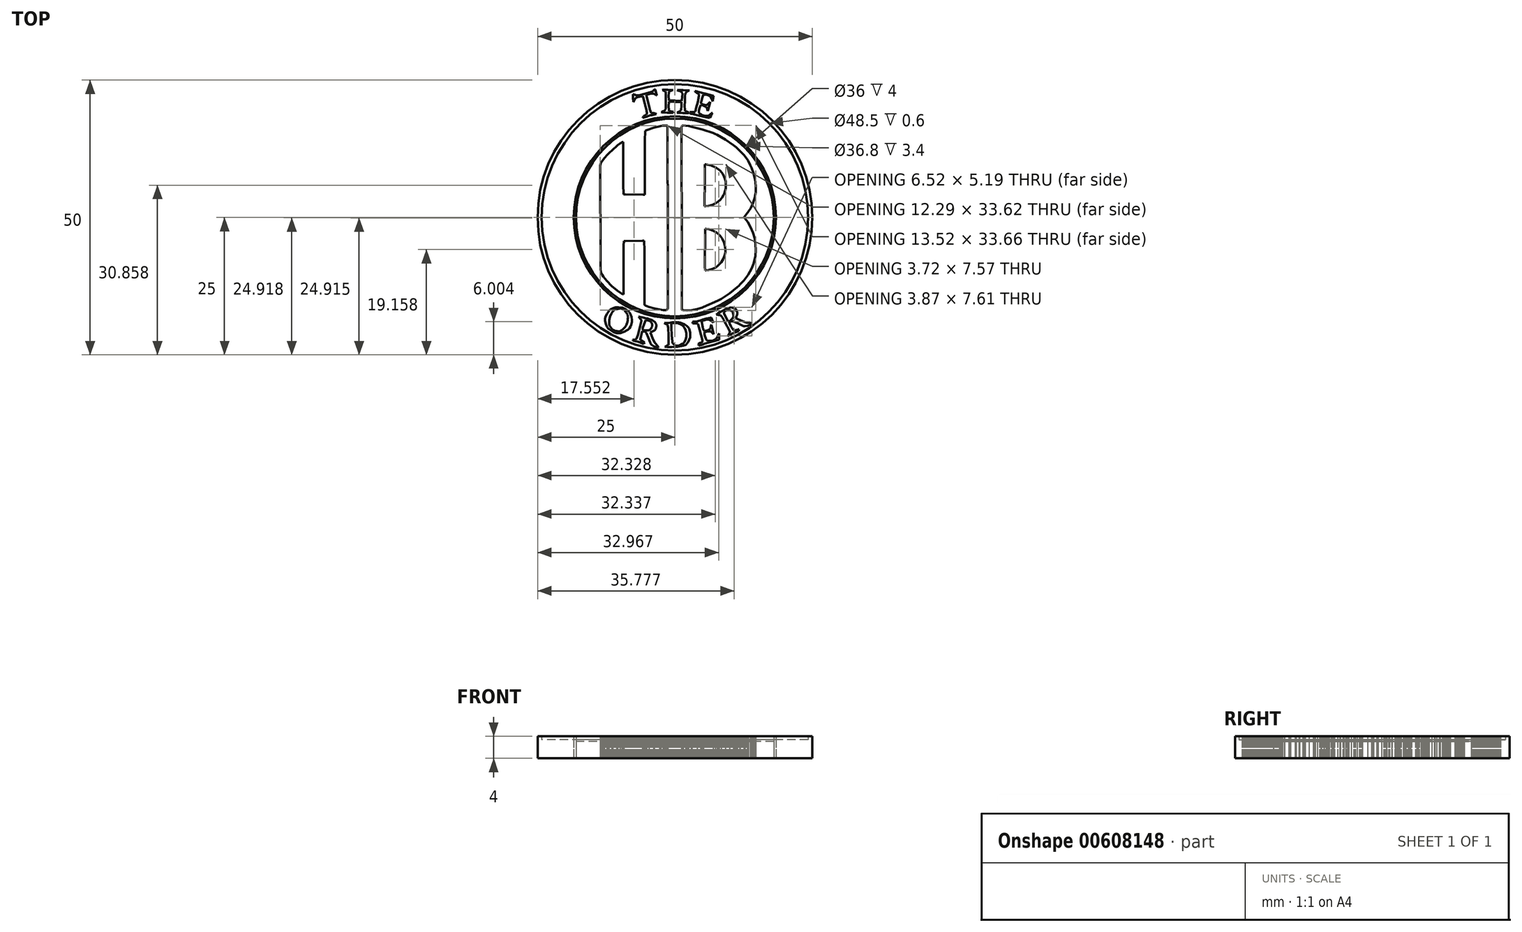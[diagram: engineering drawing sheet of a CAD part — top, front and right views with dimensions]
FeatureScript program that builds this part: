
annotation { "Feature Type Name" : "Feature", "Feature Type Description" : "" }
export const myFeature = defineFeature(function(context is Context, id is Id, definition is map)
    precondition{}
    {
        {
            var Q0;
            Q0=qCreatedBy(makeId("Top.planeOp"),FACE);
            var sketch = newSketch(context, id + "F0", { "sketchPlane" : qUnion([Q0])});
            skLineSegment(sketch, "E0", {"start": v(-4.29, 22.88) * mm, "end": v(-4.22, 22.9) * mm});
            skLineSegment(sketch, "E1", {"start": v(-4.22, 22.9) * mm, "end": v(-3.93, 23.08) * mm});
            skLineSegment(sketch, "E2", {"start": v(-3.93, 23.08) * mm, "end": v(-3.67, 23.3) * mm});
            skLineSegment(sketch, "E3", {"start": v(-3.67, 23.3) * mm, "end": v(-3.61, 23.34) * mm});
            skLineSegment(sketch, "E4", {"start": v(-3.61, 23.34) * mm, "end": v(-3.58, 23.25) * mm});
            skLineSegment(sketch, "E5", {"start": v(-3.58, 23.25) * mm, "end": v(-3.31, 22.3) * mm});
            skLineSegment(sketch, "E6", {"start": v(-3.31, 22.3) * mm, "end": v(-3.3, 22.2) * mm});
            skLineSegment(sketch, "E7", {"start": v(-3.3, 22.2) * mm, "end": v(-3.35, 22.24) * mm});
            skLineSegment(sketch, "E8", {"start": v(-3.35, 22.24) * mm, "end": v(-3.64, 22.4) * mm});
            skLineSegment(sketch, "E9", {"start": v(-3.64, 22.4) * mm, "end": v(-3.95, 22.54) * mm});
            skLineSegment(sketch, "E10", {"start": v(-3.95, 22.54) * mm, "end": v(-4.01, 22.56) * mm});
            skLineSegment(sketch, "E11", {"start": v(-4.01, 22.56) * mm, "end": v(-4.11, 22.55) * mm});
            skLineSegment(sketch, "E12", {"start": v(-4.11, 22.55) * mm, "end": v(-4.6, 22.48) * mm});
            skLineSegment(sketch, "E13", {"start": v(-4.6, 22.48) * mm, "end": v(-5.1, 22.37) * mm});
            skLineSegment(sketch, "E14", {"start": v(-5.1, 22.37) * mm, "end": v(-5.2, 22.35) * mm});
            skLineSegment(sketch, "E15", {"start": v(-5.2, 22.35) * mm, "end": v(-5.15, 22.13) * mm});
            skLineSegment(sketch, "E16", {"start": v(-5.15, 22.13) * mm, "end": v(-4.65, 20) * mm});
            skLineSegment(sketch, "E17", {"start": v(-4.65, 20) * mm, "end": v(-4.6, 19.8) * mm});
            skLineSegment(sketch, "E18", {"start": v(-4.6, 19.8) * mm, "end": v(-4.58, 19.72) * mm});
            skLineSegment(sketch, "E19", {"start": v(-4.58, 19.72) * mm, "end": v(-4.35, 19.05) * mm});
            skLineSegment(sketch, "E20", {"start": v(-4.35, 19.05) * mm, "end": v(-4.32, 18.98) * mm});
            skLineSegment(sketch, "E21", {"start": v(-4.32, 18.98) * mm, "end": v(-4.26, 18.98) * mm});
            skLineSegment(sketch, "E22", {"start": v(-4.26, 18.98) * mm, "end": v(-4.08, 18.98) * mm});
            skLineSegment(sketch, "E23", {"start": v(-4.08, 18.98) * mm, "end": v(-3.84, 18.99) * mm});
            skLineSegment(sketch, "E24", {"start": v(-3.84, 18.99) * mm, "end": v(-3.6, 18.95) * mm});
            skLineSegment(sketch, "E25", {"start": v(-3.6, 18.95) * mm, "end": v(-3.44, 18.86) * mm});
            skLineSegment(sketch, "E26", {"start": v(-3.44, 18.86) * mm, "end": v(-3.4, 18.82) * mm});
            skLineSegment(sketch, "E27", {"start": v(-3.4, 18.82) * mm, "end": v(-3.47, 18.8) * mm});
            skLineSegment(sketch, "E28", {"start": v(-3.47, 18.8) * mm, "end": v(-4.22, 18.64) * mm});
            skLineSegment(sketch, "E29", {"start": v(-4.22, 18.64) * mm, "end": v(-4.3, 18.62) * mm});
            skLineSegment(sketch, "E30", {"start": v(-4.3, 18.62) * mm, "end": v(-4.43, 18.6) * mm});
            skLineSegment(sketch, "E31", {"start": v(-4.43, 18.6) * mm, "end": v(-5.06, 18.39) * mm});
            skLineSegment(sketch, "E32", {"start": v(-5.06, 18.39) * mm, "end": v(-5.7, 18.2) * mm});
            skLineSegment(sketch, "E33", {"start": v(-5.7, 18.2) * mm, "end": v(-5.83, 18.18) * mm});
            skLineSegment(sketch, "E34", {"start": v(-5.83, 18.18) * mm, "end": v(-5.83, 18.22) * mm});
            skLineSegment(sketch, "E35", {"start": v(-5.83, 18.22) * mm, "end": v(-5.8, 18.32) * mm});
            skLineSegment(sketch, "E36", {"start": v(-5.8, 18.32) * mm, "end": v(-5.7, 18.42) * mm});
            skLineSegment(sketch, "E37", {"start": v(-5.7, 18.42) * mm, "end": v(-5.6, 18.5) * mm});
            skLineSegment(sketch, "E38", {"start": v(-5.6, 18.5) * mm, "end": v(-5.46, 18.56) * mm});
            skLineSegment(sketch, "E39", {"start": v(-5.46, 18.56) * mm, "end": v(-5.34, 18.63) * mm});
            skLineSegment(sketch, "E40", {"start": v(-5.34, 18.63) * mm, "end": v(-5.22, 18.7) * mm});
            skLineSegment(sketch, "E41", {"start": v(-5.22, 18.7) * mm, "end": v(-5.14, 18.8) * mm});
            skLineSegment(sketch, "E42", {"start": v(-5.14, 18.8) * mm, "end": v(-5.1, 18.9) * mm});
            skLineSegment(sketch, "E43", {"start": v(-5.1, 18.9) * mm, "end": v(-5.1, 18.94) * mm});
            skLineSegment(sketch, "E44", {"start": v(-5.1, 18.94) * mm, "end": v(-5.1, 19.08) * mm});
            skLineSegment(sketch, "E45", {"start": v(-5.1, 19.08) * mm, "end": v(-5.22, 19.73) * mm});
            skLineSegment(sketch, "E46", {"start": v(-5.22, 19.73) * mm, "end": v(-5.4, 20.37) * mm});
            skLineSegment(sketch, "E47", {"start": v(-5.4, 20.37) * mm, "end": v(-5.43, 20.5) * mm});
            skLineSegment(sketch, "E48", {"start": v(-5.43, 20.5) * mm, "end": v(-5.47, 20.63) * mm});
            skLineSegment(sketch, "E49", {"start": v(-5.47, 20.63) * mm, "end": v(-5.8, 21.98) * mm});
            skLineSegment(sketch, "E50", {"start": v(-5.8, 21.98) * mm, "end": v(-5.84, 22.11) * mm});
            skLineSegment(sketch, "E51", {"start": v(-5.84, 22.11) * mm, "end": v(-5.91, 22.1) * mm});
            skLineSegment(sketch, "E52", {"start": v(-5.91, 22.1) * mm, "end": v(-6.14, 22.06) * mm});
            skLineSegment(sketch, "E53", {"start": v(-6.14, 22.06) * mm, "end": v(-6.44, 22.01) * mm});
            skLineSegment(sketch, "E54", {"start": v(-6.44, 22.01) * mm, "end": v(-6.73, 21.94) * mm});
            skLineSegment(sketch, "E55", {"start": v(-6.73, 21.94) * mm, "end": v(-6.94, 21.85) * mm});
            skLineSegment(sketch, "E56", {"start": v(-6.94, 21.85) * mm, "end": v(-7, 21.81) * mm});
            skLineSegment(sketch, "E57", {"start": v(-7, 21.81) * mm, "end": v(-7.05, 21.78) * mm});
            skLineSegment(sketch, "E58", {"start": v(-7.05, 21.78) * mm, "end": v(-7.17, 21.64) * mm});
            skLineSegment(sketch, "E59", {"start": v(-7.17, 21.64) * mm, "end": v(-7.3, 21.44) * mm});
            skLineSegment(sketch, "E60", {"start": v(-7.3, 21.44) * mm, "end": v(-7.42, 21.24) * mm});
            skLineSegment(sketch, "E61", {"start": v(-7.42, 21.24) * mm, "end": v(-7.51, 21.1) * mm});
            skLineSegment(sketch, "E62", {"start": v(-7.51, 21.1) * mm, "end": v(-7.55, 21.05) * mm});
            skLineSegment(sketch, "E63", {"start": v(-7.55, 21.05) * mm, "end": v(-7.57, 21.16) * mm});
            skLineSegment(sketch, "E64", {"start": v(-7.57, 21.16) * mm, "end": v(-7.63, 21.74) * mm});
            skLineSegment(sketch, "E65", {"start": v(-7.63, 21.74) * mm, "end": v(-7.63, 22.31) * mm});
            skLineSegment(sketch, "E66", {"start": v(-7.63, 22.31) * mm, "end": v(-7.63, 22.43) * mm});
            skLineSegment(sketch, "E67", {"start": v(-7.63, 22.43) * mm, "end": v(-7.56, 22.4) * mm});
            skLineSegment(sketch, "E68", {"start": v(-7.56, 22.4) * mm, "end": v(-7.35, 22.34) * mm});
            skLineSegment(sketch, "E69", {"start": v(-7.35, 22.34) * mm, "end": v(-7.06, 22.26) * mm});
            skLineSegment(sketch, "E70", {"start": v(-7.06, 22.26) * mm, "end": v(-6.78, 22.22) * mm});
            skLineSegment(sketch, "E71", {"start": v(-6.78, 22.22) * mm, "end": v(-6.56, 22.24) * mm});
            skLineSegment(sketch, "E72", {"start": v(-6.56, 22.24) * mm, "end": v(-6.49, 22.27) * mm});
            skLineSegment(sketch, "E73", {"start": v(-6.49, 22.27) * mm, "end": v(-6.3, 22.32) * mm});
            skLineSegment(sketch, "E74", {"start": v(-6.3, 22.32) * mm, "end": v(-4.47, 22.82) * mm});
            skLineSegment(sketch, "E75", {"start": v(-4.47, 22.82) * mm, "end": v(-4.29, 22.88) * mm});
            skLineSegment(sketch, "E76", {"start": v(-2.31, 23.2) * mm, "end": v(-2.15, 23.23) * mm});
            skLineSegment(sketch, "E77", {"start": v(-2.15, 23.23) * mm, "end": v(-1.31, 23.23) * mm});
            skLineSegment(sketch, "E78", {"start": v(-1.31, 23.23) * mm, "end": v(-0.48, 23.21) * mm});
            skLineSegment(sketch, "E79", {"start": v(-0.48, 23.21) * mm, "end": v(-0.31, 23.22) * mm});
            skLineSegment(sketch, "E80", {"start": v(-0.31, 23.22) * mm, "end": v(-0.38, 23.2) * mm});
            skLineSegment(sketch, "E81", {"start": v(-0.38, 23.2) * mm, "end": v(-0.72, 23.07) * mm});
            skLineSegment(sketch, "E82", {"start": v(-0.72, 23.07) * mm, "end": v(-1.04, 22.9) * mm});
            skLineSegment(sketch, "E83", {"start": v(-1.04, 22.9) * mm, "end": v(-1.1, 22.86) * mm});
            skLineSegment(sketch, "E84", {"start": v(-1.1, 22.86) * mm, "end": v(-1.12, 22.73) * mm});
            skLineSegment(sketch, "E85", {"start": v(-1.12, 22.73) * mm, "end": v(-1.13, 22.09) * mm});
            skLineSegment(sketch, "E86", {"start": v(-1.13, 22.09) * mm, "end": v(-1.08, 21.44) * mm});
            skLineSegment(sketch, "E87", {"start": v(-1.08, 21.44) * mm, "end": v(-1.07, 21.31) * mm});
            skLineSegment(sketch, "E88", {"start": v(-1.07, 21.31) * mm, "end": v(-0.88, 21.32) * mm});
            skLineSegment(sketch, "E89", {"start": v(-0.88, 21.32) * mm, "end": v(1.03, 21.24) * mm});
            skLineSegment(sketch, "E90", {"start": v(1.03, 21.24) * mm, "end": v(1.22, 21.25) * mm});
            skLineSegment(sketch, "E91", {"start": v(1.22, 21.25) * mm, "end": v(1.23, 21.36) * mm});
            skLineSegment(sketch, "E92", {"start": v(1.23, 21.36) * mm, "end": v(1.3, 21.95) * mm});
            skLineSegment(sketch, "E93", {"start": v(1.3, 21.95) * mm, "end": v(1.35, 22.53) * mm});
            skLineSegment(sketch, "E94", {"start": v(1.35, 22.53) * mm, "end": v(1.35, 22.65) * mm});
            skLineSegment(sketch, "E95", {"start": v(1.35, 22.65) * mm, "end": v(1.33, 22.7) * mm});
            skLineSegment(sketch, "E96", {"start": v(1.33, 22.7) * mm, "end": v(1.19, 22.85) * mm});
            skLineSegment(sketch, "E97", {"start": v(1.19, 22.85) * mm, "end": v(0.95, 22.97) * mm});
            skLineSegment(sketch, "E98", {"start": v(0.95, 22.97) * mm, "end": v(0.68, 23.06) * mm});
            skLineSegment(sketch, "E99", {"start": v(0.68, 23.06) * mm, "end": v(0.5, 23.13) * mm});
            skLineSegment(sketch, "E100", {"start": v(0.5, 23.13) * mm, "end": v(0.44, 23.17) * mm});
            skLineSegment(sketch, "E101", {"start": v(0.44, 23.17) * mm, "end": v(0.62, 23.21) * mm});
            skLineSegment(sketch, "E102", {"start": v(0.62, 23.21) * mm, "end": v(1.53, 23.2) * mm});
            skLineSegment(sketch, "E103", {"start": v(1.53, 23.2) * mm, "end": v(2.45, 23.14) * mm});
            skLineSegment(sketch, "E104", {"start": v(2.45, 23.14) * mm, "end": v(2.63, 23.15) * mm});
            skLineSegment(sketch, "E105", {"start": v(2.63, 23.15) * mm, "end": v(2.58, 23.12) * mm});
            skLineSegment(sketch, "E106", {"start": v(2.58, 23.12) * mm, "end": v(2.33, 23) * mm});
            skLineSegment(sketch, "E107", {"start": v(2.33, 23) * mm, "end": v(2.08, 22.86) * mm});
            skLineSegment(sketch, "E108", {"start": v(2.08, 22.86) * mm, "end": v(2.04, 22.82) * mm});
            skLineSegment(sketch, "E109", {"start": v(2.04, 22.82) * mm, "end": v(2, 22.74) * mm});
            skLineSegment(sketch, "E110", {"start": v(2, 22.74) * mm, "end": v(1.92, 22.47) * mm});
            skLineSegment(sketch, "E111", {"start": v(1.92, 22.47) * mm, "end": v(1.86, 22.1) * mm});
            skLineSegment(sketch, "E112", {"start": v(1.86, 22.1) * mm, "end": v(1.83, 21.72) * mm});
            skLineSegment(sketch, "E113", {"start": v(1.83, 21.72) * mm, "end": v(1.82, 21.44) * mm});
            skLineSegment(sketch, "E114", {"start": v(1.82, 21.44) * mm, "end": v(1.82, 21.34) * mm});
            skLineSegment(sketch, "E115", {"start": v(1.82, 21.34) * mm, "end": v(1.82, 21.18) * mm});
            skLineSegment(sketch, "E116", {"start": v(1.82, 21.18) * mm, "end": v(1.79, 20.36) * mm});
            skLineSegment(sketch, "E117", {"start": v(1.79, 20.36) * mm, "end": v(1.8, 19.54) * mm});
            skLineSegment(sketch, "E118", {"start": v(1.8, 19.54) * mm, "end": v(1.83, 19.38) * mm});
            skLineSegment(sketch, "E119", {"start": v(1.83, 19.38) * mm, "end": v(1.89, 19.36) * mm});
            skLineSegment(sketch, "E120", {"start": v(1.89, 19.36) * mm, "end": v(2.2, 19.25) * mm});
            skLineSegment(sketch, "E121", {"start": v(2.2, 19.25) * mm, "end": v(2.5, 19.1) * mm});
            skLineSegment(sketch, "E122", {"start": v(2.5, 19.1) * mm, "end": v(2.55, 19.06) * mm});
            skLineSegment(sketch, "E123", {"start": v(2.55, 19.06) * mm, "end": v(2.37, 19.03) * mm});
            skLineSegment(sketch, "E124", {"start": v(2.37, 19.03) * mm, "end": v(1.46, 19) * mm});
            skLineSegment(sketch, "E125", {"start": v(1.46, 19) * mm, "end": v(0.55, 19.05) * mm});
            skLineSegment(sketch, "E126", {"start": v(0.55, 19.05) * mm, "end": v(0.37, 19.06) * mm});
            skLineSegment(sketch, "E127", {"start": v(0.37, 19.06) * mm, "end": v(0.41, 19.09) * mm});
            skLineSegment(sketch, "E128", {"start": v(0.41, 19.09) * mm, "end": v(0.56, 19.17) * mm});
            skLineSegment(sketch, "E129", {"start": v(0.56, 19.17) * mm, "end": v(0.76, 19.27) * mm});
            skLineSegment(sketch, "E130", {"start": v(0.76, 19.27) * mm, "end": v(0.95, 19.39) * mm});
            skLineSegment(sketch, "E131", {"start": v(0.95, 19.39) * mm, "end": v(1.08, 19.5) * mm});
            skLineSegment(sketch, "E132", {"start": v(1.08, 19.5) * mm, "end": v(1.1, 19.54) * mm});
            skLineSegment(sketch, "E133", {"start": v(1.1, 19.54) * mm, "end": v(1.13, 19.66) * mm});
            skLineSegment(sketch, "E134", {"start": v(1.13, 19.66) * mm, "end": v(1.2, 20.3) * mm});
            skLineSegment(sketch, "E135", {"start": v(1.2, 20.3) * mm, "end": v(1.2, 20.93) * mm});
            skLineSegment(sketch, "E136", {"start": v(1.2, 20.93) * mm, "end": v(1.2, 21.06) * mm});
            skLineSegment(sketch, "E137", {"start": v(1.2, 21.06) * mm, "end": v(1, 21.06) * mm});
            skLineSegment(sketch, "E138", {"start": v(1, 21.06) * mm, "end": v(0.04, 21.05) * mm});
            skLineSegment(sketch, "E139", {"start": v(0.04, 21.05) * mm, "end": v(-0.91, 21.08) * mm});
            skLineSegment(sketch, "E140", {"start": v(-0.91, 21.08) * mm, "end": v(-1.1, 21.1) * mm});
            skLineSegment(sketch, "E141", {"start": v(-1.1, 21.1) * mm, "end": v(-1.12, 20.96) * mm});
            skLineSegment(sketch, "E142", {"start": v(-1.12, 20.96) * mm, "end": v(-1.13, 20.25) * mm});
            skLineSegment(sketch, "E143", {"start": v(-1.13, 20.25) * mm, "end": v(-1.1, 19.54) * mm});
            skLineSegment(sketch, "E144", {"start": v(-1.1, 19.54) * mm, "end": v(-1.09, 19.4) * mm});
            skLineSegment(sketch, "E145", {"start": v(-1.09, 19.4) * mm, "end": v(-1.02, 19.39) * mm});
            skLineSegment(sketch, "E146", {"start": v(-1.02, 19.39) * mm, "end": v(-0.31, 19.28) * mm});
            skLineSegment(sketch, "E147", {"start": v(-0.31, 19.28) * mm, "end": v(-0.24, 19.27) * mm});
            skLineSegment(sketch, "E148", {"start": v(-0.24, 19.27) * mm, "end": v(-0.25, 19.25) * mm});
            skLineSegment(sketch, "E149", {"start": v(-0.25, 19.25) * mm, "end": v(-0.35, 19.05) * mm});
            skLineSegment(sketch, "E150", {"start": v(-0.35, 19.05) * mm, "end": v(-0.36, 19.03) * mm});
            skLineSegment(sketch, "E151", {"start": v(-0.36, 19.03) * mm, "end": v(-0.53, 19.07) * mm});
            skLineSegment(sketch, "E152", {"start": v(-0.53, 19.07) * mm, "end": v(-1.41, 19.09) * mm});
            skLineSegment(sketch, "E153", {"start": v(-1.41, 19.09) * mm, "end": v(-2.3, 19.12) * mm});
            skLineSegment(sketch, "E154", {"start": v(-2.3, 19.12) * mm, "end": v(-2.46, 19.17) * mm});
            skLineSegment(sketch, "E155", {"start": v(-2.46, 19.17) * mm, "end": v(-2.4, 19.2) * mm});
            skLineSegment(sketch, "E156", {"start": v(-2.4, 19.2) * mm, "end": v(-2.23, 19.29) * mm});
            skLineSegment(sketch, "E157", {"start": v(-2.23, 19.29) * mm, "end": v(-1.97, 19.4) * mm});
            skLineSegment(sketch, "E158", {"start": v(-1.97, 19.4) * mm, "end": v(-1.77, 19.55) * mm});
            skLineSegment(sketch, "E159", {"start": v(-1.77, 19.55) * mm, "end": v(-1.68, 19.73) * mm});
            skLineSegment(sketch, "E160", {"start": v(-1.68, 19.73) * mm, "end": v(-1.68, 19.8) * mm});
            skLineSegment(sketch, "E161", {"start": v(-1.68, 19.8) * mm, "end": v(-1.66, 20.06) * mm});
            skLineSegment(sketch, "E162", {"start": v(-1.66, 20.06) * mm, "end": v(-1.64, 21.37) * mm});
            skLineSegment(sketch, "E163", {"start": v(-1.64, 21.37) * mm, "end": v(-1.7, 22.68) * mm});
            skLineSegment(sketch, "E164", {"start": v(-1.7, 22.68) * mm, "end": v(-1.7, 22.94) * mm});
            skLineSegment(sketch, "E165", {"start": v(-1.7, 22.94) * mm, "end": v(-1.76, 22.96) * mm});
            skLineSegment(sketch, "E166", {"start": v(-1.76, 22.96) * mm, "end": v(-2.26, 23.19) * mm});
            skLineSegment(sketch, "E167", {"start": v(-2.26, 23.19) * mm, "end": v(-2.31, 23.2) * mm});
            skLineSegment(sketch, "E168", {"start": v(3.67, 23.01) * mm, "end": v(3.82, 23) * mm});
            skLineSegment(sketch, "E169", {"start": v(3.82, 23) * mm, "end": v(4.51, 22.8) * mm});
            skLineSegment(sketch, "E170", {"start": v(4.51, 22.8) * mm, "end": v(5.2, 22.6) * mm});
            skLineSegment(sketch, "E171", {"start": v(5.2, 22.6) * mm, "end": v(5.35, 22.58) * mm});
            skLineSegment(sketch, "E172", {"start": v(5.35, 22.58) * mm, "end": v(5.5, 22.56) * mm});
            skLineSegment(sketch, "E173", {"start": v(5.5, 22.56) * mm, "end": v(6.2, 22.38) * mm});
            skLineSegment(sketch, "E174", {"start": v(6.2, 22.38) * mm, "end": v(6.9, 22.14) * mm});
            skLineSegment(sketch, "E175", {"start": v(6.9, 22.14) * mm, "end": v(7.03, 22.1) * mm});
            skLineSegment(sketch, "E176", {"start": v(7.03, 22.1) * mm, "end": v(7.02, 22.02) * mm});
            skLineSegment(sketch, "E177", {"start": v(7.02, 22.02) * mm, "end": v(6.9, 21.26) * mm});
            skLineSegment(sketch, "E178", {"start": v(6.9, 21.26) * mm, "end": v(6.88, 21.19) * mm});
            skLineSegment(sketch, "E179", {"start": v(6.88, 21.19) * mm, "end": v(6.85, 21.25) * mm});
            skLineSegment(sketch, "E180", {"start": v(6.85, 21.25) * mm, "end": v(6.7, 21.6) * mm});
            skLineSegment(sketch, "E181", {"start": v(6.7, 21.6) * mm, "end": v(6.53, 21.92) * mm});
            skLineSegment(sketch, "E182", {"start": v(6.53, 21.92) * mm, "end": v(6.48, 21.97) * mm});
            skLineSegment(sketch, "E183", {"start": v(6.48, 21.97) * mm, "end": v(6.42, 22.03) * mm});
            skLineSegment(sketch, "E184", {"start": v(6.42, 22.03) * mm, "end": v(6.2, 22.16) * mm});
            skLineSegment(sketch, "E185", {"start": v(6.2, 22.16) * mm, "end": v(5.87, 22.28) * mm});
            skLineSegment(sketch, "E186", {"start": v(5.87, 22.28) * mm, "end": v(5.53, 22.35) * mm});
            skLineSegment(sketch, "E187", {"start": v(5.53, 22.35) * mm, "end": v(5.27, 22.37) * mm});
            skLineSegment(sketch, "E188", {"start": v(5.27, 22.37) * mm, "end": v(5.18, 22.37) * mm});
            skLineSegment(sketch, "E189", {"start": v(5.18, 22.37) * mm, "end": v(5.15, 22.25) * mm});
            skLineSegment(sketch, "E190", {"start": v(5.15, 22.25) * mm, "end": v(4.95, 21.67) * mm});
            skLineSegment(sketch, "E191", {"start": v(4.95, 21.67) * mm, "end": v(4.8, 21.08) * mm});
            skLineSegment(sketch, "E192", {"start": v(4.8, 21.08) * mm, "end": v(4.77, 20.95) * mm});
            skLineSegment(sketch, "E193", {"start": v(4.77, 20.95) * mm, "end": v(4.77, 20.9) * mm});
            skLineSegment(sketch, "E194", {"start": v(4.77, 20.9) * mm, "end": v(4.84, 20.7) * mm});
            skLineSegment(sketch, "E195", {"start": v(4.84, 20.7) * mm, "end": v(5.05, 20.57) * mm});
            skLineSegment(sketch, "E196", {"start": v(5.05, 20.57) * mm, "end": v(5.32, 20.51) * mm});
            skLineSegment(sketch, "E197", {"start": v(5.32, 20.51) * mm, "end": v(5.5, 20.49) * mm});
            skLineSegment(sketch, "E198", {"start": v(5.5, 20.49) * mm, "end": v(5.57, 20.48) * mm});
            skLineSegment(sketch, "E199", {"start": v(5.57, 20.48) * mm, "end": v(5.63, 20.46) * mm});
            skLineSegment(sketch, "E200", {"start": v(5.63, 20.46) * mm, "end": v(5.83, 20.49) * mm});
            skLineSegment(sketch, "E201", {"start": v(5.83, 20.49) * mm, "end": v(6.04, 20.63) * mm});
            skLineSegment(sketch, "E202", {"start": v(6.04, 20.63) * mm, "end": v(6.23, 20.82) * mm});
            skLineSegment(sketch, "E203", {"start": v(6.23, 20.82) * mm, "end": v(6.36, 20.97) * mm});
            skLineSegment(sketch, "E204", {"start": v(6.36, 20.97) * mm, "end": v(6.4, 21) * mm});
            skLineSegment(sketch, "E205", {"start": v(6.4, 21) * mm, "end": v(6.37, 20.87) * mm});
            skLineSegment(sketch, "E206", {"start": v(6.37, 20.87) * mm, "end": v(6, 19.52) * mm});
            skLineSegment(sketch, "E207", {"start": v(6, 19.52) * mm, "end": v(5.96, 19.38) * mm});
            skLineSegment(sketch, "E208", {"start": v(5.96, 19.38) * mm, "end": v(5.94, 19.44) * mm});
            skLineSegment(sketch, "E209", {"start": v(5.94, 19.44) * mm, "end": v(5.86, 19.74) * mm});
            skLineSegment(sketch, "E210", {"start": v(5.86, 19.74) * mm, "end": v(5.76, 20.02) * mm});
            skLineSegment(sketch, "E211", {"start": v(5.76, 20.02) * mm, "end": v(5.73, 20.07) * mm});
            skLineSegment(sketch, "E212", {"start": v(5.73, 20.07) * mm, "end": v(5.68, 20.12) * mm});
            skLineSegment(sketch, "E213", {"start": v(5.68, 20.12) * mm, "end": v(5.5, 20.24) * mm});
            skLineSegment(sketch, "E214", {"start": v(5.5, 20.24) * mm, "end": v(5.25, 20.35) * mm});
            skLineSegment(sketch, "E215", {"start": v(5.25, 20.35) * mm, "end": v(4.98, 20.44) * mm});
            skLineSegment(sketch, "E216", {"start": v(4.98, 20.44) * mm, "end": v(4.77, 20.49) * mm});
            skLineSegment(sketch, "E217", {"start": v(4.77, 20.49) * mm, "end": v(4.7, 20.5) * mm});
            skLineSegment(sketch, "E218", {"start": v(4.7, 20.5) * mm, "end": v(4.67, 20.42) * mm});
            skLineSegment(sketch, "E219", {"start": v(4.67, 20.42) * mm, "end": v(4.57, 20.15) * mm});
            skLineSegment(sketch, "E220", {"start": v(4.57, 20.15) * mm, "end": v(4.46, 19.79) * mm});
            skLineSegment(sketch, "E221", {"start": v(4.46, 19.79) * mm, "end": v(4.4, 19.42) * mm});
            skLineSegment(sketch, "E222", {"start": v(4.4, 19.42) * mm, "end": v(4.39, 19.13) * mm});
            skLineSegment(sketch, "E223", {"start": v(4.39, 19.13) * mm, "end": v(4.4, 19.04) * mm});
            skLineSegment(sketch, "E224", {"start": v(4.4, 19.04) * mm, "end": v(4.44, 18.97) * mm});
            skLineSegment(sketch, "E225", {"start": v(4.44, 18.97) * mm, "end": v(4.62, 18.79) * mm});
            skLineSegment(sketch, "E226", {"start": v(4.62, 18.79) * mm, "end": v(4.92, 18.63) * mm});
            skLineSegment(sketch, "E227", {"start": v(4.92, 18.63) * mm, "end": v(5.26, 18.54) * mm});
            skLineSegment(sketch, "E228", {"start": v(5.26, 18.54) * mm, "end": v(5.51, 18.5) * mm});
            skLineSegment(sketch, "E229", {"start": v(5.51, 18.5) * mm, "end": v(5.6, 18.48) * mm});
            skLineSegment(sketch, "E230", {"start": v(5.6, 18.48) * mm, "end": v(5.68, 18.46) * mm});
            skLineSegment(sketch, "E231", {"start": v(5.68, 18.46) * mm, "end": v(5.94, 18.5) * mm});
            skLineSegment(sketch, "E232", {"start": v(5.94, 18.5) * mm, "end": v(6.25, 18.64) * mm});
            skLineSegment(sketch, "E233", {"start": v(6.25, 18.64) * mm, "end": v(6.54, 18.85) * mm});
            skLineSegment(sketch, "E234", {"start": v(6.54, 18.85) * mm, "end": v(6.75, 19) * mm});
            skLineSegment(sketch, "E235", {"start": v(6.75, 19) * mm, "end": v(6.82, 19.06) * mm});
            skLineSegment(sketch, "E236", {"start": v(6.82, 19.06) * mm, "end": v(6.78, 18.98) * mm});
            skLineSegment(sketch, "E237", {"start": v(6.78, 18.98) * mm, "end": v(6.6, 18.58) * mm});
            skLineSegment(sketch, "E238", {"start": v(6.6, 18.58) * mm, "end": v(6.37, 18.2) * mm});
            skLineSegment(sketch, "E239", {"start": v(6.37, 18.2) * mm, "end": v(6.31, 18.14) * mm});
            skLineSegment(sketch, "E240", {"start": v(6.31, 18.14) * mm, "end": v(6.02, 18.18) * mm});
            skLineSegment(sketch, "E241", {"start": v(6.02, 18.18) * mm, "end": v(4.57, 18.52) * mm});
            skLineSegment(sketch, "E242", {"start": v(4.57, 18.52) * mm, "end": v(3.11, 18.85) * mm});
            skLineSegment(sketch, "E243", {"start": v(3.11, 18.85) * mm, "end": v(2.81, 18.88) * mm});
            skLineSegment(sketch, "E244", {"start": v(2.81, 18.88) * mm, "end": v(2.8, 18.9) * mm});
            skLineSegment(sketch, "E245", {"start": v(2.8, 18.9) * mm, "end": v(2.73, 19.18) * mm});
            skLineSegment(sketch, "E246", {"start": v(2.73, 19.18) * mm, "end": v(2.72, 19.2) * mm});
            skLineSegment(sketch, "E247", {"start": v(2.72, 19.2) * mm, "end": v(2.79, 19.2) * mm});
            skLineSegment(sketch, "E248", {"start": v(2.79, 19.2) * mm, "end": v(3.12, 19.19) * mm});
            skLineSegment(sketch, "E249", {"start": v(3.12, 19.19) * mm, "end": v(3.45, 19.2) * mm});
            skLineSegment(sketch, "E250", {"start": v(3.45, 19.2) * mm, "end": v(3.52, 19.2) * mm});
            skLineSegment(sketch, "E251", {"start": v(3.52, 19.2) * mm, "end": v(3.56, 19.2) * mm});
            skLineSegment(sketch, "E252", {"start": v(3.56, 19.2) * mm, "end": v(3.66, 19.27) * mm});
            skLineSegment(sketch, "E253", {"start": v(3.66, 19.27) * mm, "end": v(3.73, 19.4) * mm});
            skLineSegment(sketch, "E254", {"start": v(3.73, 19.4) * mm, "end": v(3.78, 19.56) * mm});
            skLineSegment(sketch, "E255", {"start": v(3.78, 19.56) * mm, "end": v(3.8, 19.68) * mm});
            skLineSegment(sketch, "E256", {"start": v(3.8, 19.68) * mm, "end": v(3.82, 19.71) * mm});
            skLineSegment(sketch, "E257", {"start": v(3.82, 19.71) * mm, "end": v(3.86, 19.94) * mm});
            skLineSegment(sketch, "E258", {"start": v(3.86, 19.94) * mm, "end": v(4.17, 21.03) * mm});
            skLineSegment(sketch, "E259", {"start": v(4.17, 21.03) * mm, "end": v(4.4, 22.14) * mm});
            skLineSegment(sketch, "E260", {"start": v(4.4, 22.14) * mm, "end": v(4.4, 22.37) * mm});
            skLineSegment(sketch, "E261", {"start": v(4.4, 22.37) * mm, "end": v(4.36, 22.42) * mm});
            skLineSegment(sketch, "E262", {"start": v(4.36, 22.42) * mm, "end": v(4.22, 22.53) * mm});
            skLineSegment(sketch, "E263", {"start": v(4.22, 22.53) * mm, "end": v(4.01, 22.66) * mm});
            skLineSegment(sketch, "E264", {"start": v(4.01, 22.66) * mm, "end": v(3.81, 22.8) * mm});
            skLineSegment(sketch, "E265", {"start": v(3.81, 22.8) * mm, "end": v(3.7, 22.96) * mm});
            skLineSegment(sketch, "E266", {"start": v(3.7, 22.96) * mm, "end": v(3.67, 23.01) * mm});
            skLineSegment(sketch, "E267", {"start": v(1.35, 16.73) * mm, "end": v(1.46, 16.75) * mm});
            skLineSegment(sketch, "E268", {"start": v(1.46, 16.75) * mm, "end": v(1.97, 16.73) * mm});
            skLineSegment(sketch, "E269", {"start": v(1.97, 16.73) * mm, "end": v(2.48, 16.64) * mm});
            skLineSegment(sketch, "E270", {"start": v(2.48, 16.64) * mm, "end": v(2.58, 16.62) * mm});
            skLineSegment(sketch, "E271", {"start": v(2.58, 16.62) * mm, "end": v(2.99, 16.54) * mm});
            skLineSegment(sketch, "E272", {"start": v(2.99, 16.54) * mm, "end": v(5, 16.03) * mm});
            skLineSegment(sketch, "E273", {"start": v(5, 16.03) * mm, "end": v(6.96, 15.35) * mm});
            skLineSegment(sketch, "E274", {"start": v(6.96, 15.35) * mm, "end": v(7.34, 15.19) * mm});
            skLineSegment(sketch, "E275", {"start": v(7.34, 15.19) * mm, "end": v(7.67, 15.04) * mm});
            skLineSegment(sketch, "E276", {"start": v(7.67, 15.04) * mm, "end": v(9.2, 14.18) * mm});
            skLineSegment(sketch, "E277", {"start": v(9.2, 14.18) * mm, "end": v(10.63, 13.16) * mm});
            skLineSegment(sketch, "E278", {"start": v(10.63, 13.16) * mm, "end": v(10.9, 12.94) * mm});
            skLineSegment(sketch, "E279", {"start": v(10.9, 12.94) * mm, "end": v(11.13, 12.75) * mm});
            skLineSegment(sketch, "E280", {"start": v(11.13, 12.75) * mm, "end": v(11.79, 12.15) * mm});
            skLineSegment(sketch, "E281", {"start": v(11.79, 12.15) * mm, "end": v(12.6, 11.3) * mm});
            skLineSegment(sketch, "E282", {"start": v(12.6, 11.3) * mm, "end": v(13.3, 10.34) * mm});
            skLineSegment(sketch, "E283", {"start": v(13.3, 10.34) * mm, "end": v(13.73, 9.56) * mm});
            skLineSegment(sketch, "E284", {"start": v(13.73, 9.56) * mm, "end": v(13.83, 9.28) * mm});
            skLineSegment(sketch, "E285", {"start": v(13.83, 9.28) * mm, "end": v(13.95, 9) * mm});
            skLineSegment(sketch, "E286", {"start": v(13.95, 9) * mm, "end": v(14.26, 8.14) * mm});
            skLineSegment(sketch, "E287", {"start": v(14.26, 8.14) * mm, "end": v(14.56, 6.96) * mm});
            skLineSegment(sketch, "E288", {"start": v(14.56, 6.96) * mm, "end": v(14.71, 5.75) * mm});
            skLineSegment(sketch, "E289", {"start": v(14.71, 5.75) * mm, "end": v(14.73, 4.83) * mm});
            skLineSegment(sketch, "E290", {"start": v(14.73, 4.83) * mm, "end": v(14.7, 4.53) * mm});
            skLineSegment(sketch, "E291", {"start": v(14.7, 4.53) * mm, "end": v(14.67, 4.28) * mm});
            skLineSegment(sketch, "E292", {"start": v(14.67, 4.28) * mm, "end": v(14.53, 3.55) * mm});
            skLineSegment(sketch, "E293", {"start": v(14.53, 3.55) * mm, "end": v(14.24, 2.6) * mm});
            skLineSegment(sketch, "E294", {"start": v(14.24, 2.6) * mm, "end": v(13.81, 1.7) * mm});
            skLineSegment(sketch, "E295", {"start": v(13.81, 1.7) * mm, "end": v(13.4, 1.07) * mm});
            skLineSegment(sketch, "E296", {"start": v(13.4, 1.07) * mm, "end": v(13.24, 0.89) * mm});
            skLineSegment(sketch, "E297", {"start": v(13.24, 0.89) * mm, "end": v(13.19, 0.82) * mm});
            skLineSegment(sketch, "E298", {"start": v(13.19, 0.82) * mm, "end": v(12.63, 0.1) * mm});
            skLineSegment(sketch, "E299", {"start": v(12.63, 0.1) * mm, "end": v(12.57, 0.03) * mm});
            skLineSegment(sketch, "E300", {"start": v(12.57, 0.03) * mm, "end": v(12.75, -0.17) * mm});
            skLineSegment(sketch, "E301", {"start": v(12.75, -0.17) * mm, "end": v(13.23, -0.83) * mm});
            skLineSegment(sketch, "E302", {"start": v(13.23, -0.83) * mm, "end": v(13.78, -1.76) * mm});
            skLineSegment(sketch, "E303", {"start": v(13.78, -1.76) * mm, "end": v(14.2, -2.76) * mm});
            skLineSegment(sketch, "E304", {"start": v(14.2, -2.76) * mm, "end": v(14.5, -3.8) * mm});
            skLineSegment(sketch, "E305", {"start": v(14.5, -3.8) * mm, "end": v(14.68, -4.87) * mm});
            skLineSegment(sketch, "E306", {"start": v(14.68, -4.87) * mm, "end": v(14.73, -5.95) * mm});
            skLineSegment(sketch, "E307", {"start": v(14.73, -5.95) * mm, "end": v(14.63, -7.03) * mm});
            skLineSegment(sketch, "E308", {"start": v(14.63, -7.03) * mm, "end": v(14.47, -7.82) * mm});
            skLineSegment(sketch, "E309", {"start": v(14.47, -7.82) * mm, "end": v(14.4, -8.08) * mm});
            skLineSegment(sketch, "E310", {"start": v(14.4, -8.08) * mm, "end": v(14.3, -8.4) * mm});
            skLineSegment(sketch, "E311", {"start": v(14.3, -8.4) * mm, "end": v(13.96, -9.3) * mm});
            skLineSegment(sketch, "E312", {"start": v(13.96, -9.3) * mm, "end": v(13.33, -10.45) * mm});
            skLineSegment(sketch, "E313", {"start": v(13.33, -10.45) * mm, "end": v(12.55, -11.49) * mm});
            skLineSegment(sketch, "E314", {"start": v(12.55, -11.49) * mm, "end": v(11.89, -12.2) * mm});
            skLineSegment(sketch, "E315", {"start": v(11.89, -12.2) * mm, "end": v(11.65, -12.42) * mm});
            skLineSegment(sketch, "E316", {"start": v(11.65, -12.42) * mm, "end": v(11.37, -12.67) * mm});
            skLineSegment(sketch, "E317", {"start": v(11.37, -12.67) * mm, "end": v(9.95, -13.85) * mm});
            skLineSegment(sketch, "E318", {"start": v(9.95, -13.85) * mm, "end": v(8.4, -14.87) * mm});
            skLineSegment(sketch, "E319", {"start": v(8.4, -14.87) * mm, "end": v(8.08, -15.05) * mm});
            skLineSegment(sketch, "E320", {"start": v(8.08, -15.05) * mm, "end": v(7.82, -15.17) * mm});
            skLineSegment(sketch, "E321", {"start": v(7.82, -15.17) * mm, "end": v(5.18, -16.33) * mm});
            skLineSegment(sketch, "E322", {"start": v(5.18, -16.33) * mm, "end": v(4.91, -16.43) * mm});
            skLineSegment(sketch, "E323", {"start": v(4.91, -16.43) * mm, "end": v(4.69, -16.5) * mm});
            skLineSegment(sketch, "E324", {"start": v(4.69, -16.5) * mm, "end": v(4.02, -16.68) * mm});
            skLineSegment(sketch, "E325", {"start": v(4.02, -16.68) * mm, "end": v(3.1, -16.85) * mm});
            skLineSegment(sketch, "E326", {"start": v(3.1, -16.85) * mm, "end": v(2.19, -16.92) * mm});
            skLineSegment(sketch, "E327", {"start": v(2.19, -16.92) * mm, "end": v(1.5, -16.88) * mm});
            skLineSegment(sketch, "E328", {"start": v(1.5, -16.88) * mm, "end": v(1.27, -16.84) * mm});
            skLineSegment(sketch, "E329", {"start": v(1.27, -16.84) * mm, "end": v(1.25, -15.43) * mm});
            skLineSegment(sketch, "E330", {"start": v(1.25, -15.43) * mm, "end": v(1.24, -1.27) * mm});
            skLineSegment(sketch, "E331", {"start": v(1.24, -1.27) * mm, "end": v(1.23, 0.15) * mm});
            skLineSegment(sketch, "E332", {"start": v(1.23, 0.15) * mm, "end": v(1.24, 0.9) * mm});
            skLineSegment(sketch, "E333", {"start": v(1.24, 0.9) * mm, "end": v(1.2, 8.4) * mm});
            skLineSegment(sketch, "E334", {"start": v(1.2, 8.4) * mm, "end": v(1.2, 9.15) * mm});
            skLineSegment(sketch, "E335", {"start": v(1.2, 9.15) * mm, "end": v(1.2, 10.94) * mm});
            skLineSegment(sketch, "E336", {"start": v(1.2, 10.94) * mm, "end": v(1.2, 15.72) * mm});
            skLineSegment(sketch, "E337", {"start": v(1.2, 15.72) * mm, "end": v(1.2, 16.31) * mm});
            skLineSegment(sketch, "E338", {"start": v(1.2, 16.31) * mm, "end": v(1.21, 16.34) * mm});
            skLineSegment(sketch, "E339", {"start": v(1.21, 16.34) * mm, "end": v(1.21, 16.43) * mm});
            skLineSegment(sketch, "E340", {"start": v(1.21, 16.43) * mm, "end": v(1.22, 16.55) * mm});
            skLineSegment(sketch, "E341", {"start": v(1.22, 16.55) * mm, "end": v(1.26, 16.66) * mm});
            skLineSegment(sketch, "E342", {"start": v(1.26, 16.66) * mm, "end": v(1.33, 16.72) * mm});
            skLineSegment(sketch, "E343", {"start": v(1.33, 16.72) * mm, "end": v(1.35, 16.73) * mm});
            skLineSegment(sketch, "E344", {"start": v(-5.4, 15.76) * mm, "end": v(-5.16, 15.88) * mm});
            skLineSegment(sketch, "E345", {"start": v(-5.16, 15.88) * mm, "end": v(-3.87, 16.34) * mm});
            skLineSegment(sketch, "E346", {"start": v(-3.87, 16.34) * mm, "end": v(-2.52, 16.64) * mm});
            skLineSegment(sketch, "E347", {"start": v(-2.52, 16.64) * mm, "end": v(-2.25, 16.68) * mm});
            skLineSegment(sketch, "E348", {"start": v(-2.25, 16.68) * mm, "end": v(-2.18, 16.7) * mm});
            skLineSegment(sketch, "E349", {"start": v(-2.18, 16.7) * mm, "end": v(-1.41, 16.73) * mm});
            skLineSegment(sketch, "E350", {"start": v(-1.41, 16.73) * mm, "end": v(-1.34, 16.73) * mm});
            skLineSegment(sketch, "E351", {"start": v(-1.34, 16.73) * mm, "end": v(-1.33, 15.8) * mm});
            skLineSegment(sketch, "E352", {"start": v(-1.33, 15.8) * mm, "end": v(-1.32, 6.58) * mm});
            skLineSegment(sketch, "E353", {"start": v(-1.32, 6.58) * mm, "end": v(-1.3, 5.66) * mm});
            skLineSegment(sketch, "E354", {"start": v(-1.3, 5.66) * mm, "end": v(-1.3, 3.81) * mm});
            skLineSegment(sketch, "E355", {"start": v(-1.3, 3.81) * mm, "end": v(-1.3, -14.66) * mm});
            skLineSegment(sketch, "E356", {"start": v(-1.3, -14.66) * mm, "end": v(-1.31, -16.5) * mm});
            skLineSegment(sketch, "E357", {"start": v(-1.31, -16.5) * mm, "end": v(-1.3, -16.55) * mm});
            skLineSegment(sketch, "E358", {"start": v(-1.3, -16.55) * mm, "end": v(-1.34, -16.71) * mm});
            skLineSegment(sketch, "E359", {"start": v(-1.34, -16.71) * mm, "end": v(-1.48, -16.84) * mm});
            skLineSegment(sketch, "E360", {"start": v(-1.48, -16.84) * mm, "end": v(-1.68, -16.9) * mm});
            skLineSegment(sketch, "E361", {"start": v(-1.68, -16.9) * mm, "end": v(-1.84, -16.9) * mm});
            skLineSegment(sketch, "E362", {"start": v(-1.84, -16.9) * mm, "end": v(-1.89, -16.88) * mm});
            skLineSegment(sketch, "E363", {"start": v(-1.89, -16.88) * mm, "end": v(-2.12, -16.86) * mm});
            skLineSegment(sketch, "E364", {"start": v(-2.12, -16.86) * mm, "end": v(-2.83, -16.76) * mm});
            skLineSegment(sketch, "E365", {"start": v(-2.83, -16.76) * mm, "end": v(-3.77, -16.59) * mm});
            skLineSegment(sketch, "E366", {"start": v(-3.77, -16.59) * mm, "end": v(-4.69, -16.32) * mm});
            skLineSegment(sketch, "E367", {"start": v(-4.69, -16.32) * mm, "end": v(-5.35, -16.05) * mm});
            skLineSegment(sketch, "E368", {"start": v(-5.35, -16.05) * mm, "end": v(-5.56, -15.94) * mm});
            skLineSegment(sketch, "E369", {"start": v(-5.56, -15.94) * mm, "end": v(-5.54, -15.22) * mm});
            skLineSegment(sketch, "E370", {"start": v(-5.54, -15.22) * mm, "end": v(-5.52, -8.02) * mm});
            skLineSegment(sketch, "E371", {"start": v(-5.52, -8.02) * mm, "end": v(-5.52, -7.3) * mm});
            skLineSegment(sketch, "E372", {"start": v(-5.52, -7.3) * mm, "end": v(-5.53, -7.05) * mm});
            skLineSegment(sketch, "E373", {"start": v(-5.53, -7.05) * mm, "end": v(-5.54, -5.78) * mm});
            skLineSegment(sketch, "E374", {"start": v(-5.54, -5.78) * mm, "end": v(-5.59, -4.51) * mm});
            skLineSegment(sketch, "E375", {"start": v(-5.59, -4.51) * mm, "end": v(-5.62, -4.26) * mm});
            skLineSegment(sketch, "E376", {"start": v(-5.62, -4.26) * mm, "end": v(-5.93, -4.26) * mm});
            skLineSegment(sketch, "E377", {"start": v(-5.93, -4.26) * mm, "end": v(-9, -4.33) * mm});
            skLineSegment(sketch, "E378", {"start": v(-9, -4.33) * mm, "end": v(-9.3, -4.34) * mm});
            skLineSegment(sketch, "E379", {"start": v(-9.3, -4.34) * mm, "end": v(-9.32, -5.14) * mm});
            skLineSegment(sketch, "E380", {"start": v(-9.32, -5.14) * mm, "end": v(-9.34, -13.22) * mm});
            skLineSegment(sketch, "E381", {"start": v(-9.34, -13.22) * mm, "end": v(-9.36, -14.03) * mm});
            skLineSegment(sketch, "E382", {"start": v(-9.36, -14.03) * mm, "end": v(-9.65, -13.88) * mm});
            skLineSegment(sketch, "E383", {"start": v(-9.65, -13.88) * mm, "end": v(-10.48, -13.34) * mm});
            skLineSegment(sketch, "E384", {"start": v(-10.48, -13.34) * mm, "end": v(-11.49, -12.5) * mm});
            skLineSegment(sketch, "E385", {"start": v(-11.49, -12.5) * mm, "end": v(-12.4, -11.54) * mm});
            skLineSegment(sketch, "E386", {"start": v(-12.4, -11.54) * mm, "end": v(-13.02, -10.77) * mm});
            skLineSegment(sketch, "E387", {"start": v(-13.02, -10.77) * mm, "end": v(-13.2, -10.5) * mm});
            skLineSegment(sketch, "E388", {"start": v(-13.2, -10.5) * mm, "end": v(-13.3, -10.38) * mm});
            skLineSegment(sketch, "E389", {"start": v(-13.3, -10.38) * mm, "end": v(-13.47, -9.96) * mm});
            skLineSegment(sketch, "E390", {"start": v(-13.47, -9.96) * mm, "end": v(-13.55, -9.38) * mm});
            skLineSegment(sketch, "E391", {"start": v(-13.55, -9.38) * mm, "end": v(-13.55, -8.77) * mm});
            skLineSegment(sketch, "E392", {"start": v(-13.55, -8.77) * mm, "end": v(-13.53, -8.33) * mm});
            skLineSegment(sketch, "E393", {"start": v(-13.53, -8.33) * mm, "end": v(-13.53, -8.18) * mm});
            skLineSegment(sketch, "E394", {"start": v(-13.53, -8.18) * mm, "end": v(-13.53, -7.41) * mm});
            skLineSegment(sketch, "E395", {"start": v(-13.53, -7.41) * mm, "end": v(-13.56, 0.25) * mm});
            skLineSegment(sketch, "E396", {"start": v(-13.56, 0.25) * mm, "end": v(-13.57, 1.02) * mm});
            skLineSegment(sketch, "E397", {"start": v(-13.57, 1.02) * mm, "end": v(-13.57, 1.67) * mm});
            skLineSegment(sketch, "E398", {"start": v(-13.57, 1.67) * mm, "end": v(-13.57, 8.2) * mm});
            skLineSegment(sketch, "E399", {"start": v(-13.57, 8.2) * mm, "end": v(-13.58, 8.85) * mm});
            skLineSegment(sketch, "E400", {"start": v(-13.58, 8.85) * mm, "end": v(-13.58, 8.92) * mm});
            skLineSegment(sketch, "E401", {"start": v(-13.58, 8.92) * mm, "end": v(-13.58, 9.14) * mm});
            skLineSegment(sketch, "E402", {"start": v(-13.58, 9.14) * mm, "end": v(-13.6, 9.43) * mm});
            skLineSegment(sketch, "E403", {"start": v(-13.6, 9.43) * mm, "end": v(-13.57, 9.71) * mm});
            skLineSegment(sketch, "E404", {"start": v(-13.57, 9.71) * mm, "end": v(-13.5, 9.92) * mm});
            skLineSegment(sketch, "E405", {"start": v(-13.5, 9.92) * mm, "end": v(-13.46, 9.98) * mm});
            skLineSegment(sketch, "E406", {"start": v(-13.46, 9.98) * mm, "end": v(-13.38, 10.13) * mm});
            skLineSegment(sketch, "E407", {"start": v(-13.38, 10.13) * mm, "end": v(-12.85, 10.8) * mm});
            skLineSegment(sketch, "E408", {"start": v(-12.85, 10.8) * mm, "end": v(-12.26, 11.44) * mm});
            skLineSegment(sketch, "E409", {"start": v(-12.26, 11.44) * mm, "end": v(-12.14, 11.56) * mm});
            skLineSegment(sketch, "E410", {"start": v(-12.14, 11.56) * mm, "end": v(-12.02, 11.7) * mm});
            skLineSegment(sketch, "E411", {"start": v(-12.02, 11.7) * mm, "end": v(-11.34, 12.35) * mm});
            skLineSegment(sketch, "E412", {"start": v(-11.34, 12.35) * mm, "end": v(-10.62, 12.97) * mm});
            skLineSegment(sketch, "E413", {"start": v(-10.62, 12.97) * mm, "end": v(-10.48, 13.1) * mm});
            skLineSegment(sketch, "E414", {"start": v(-10.48, 13.1) * mm, "end": v(-10.4, 13.17) * mm});
            skLineSegment(sketch, "E415", {"start": v(-10.4, 13.17) * mm, "end": v(-9.98, 13.47) * mm});
            skLineSegment(sketch, "E416", {"start": v(-9.98, 13.47) * mm, "end": v(-9.52, 13.71) * mm});
            skLineSegment(sketch, "E417", {"start": v(-9.52, 13.71) * mm, "end": v(-9.42, 13.75) * mm});
            skLineSegment(sketch, "E418", {"start": v(-9.42, 13.75) * mm, "end": v(-9.41, 13.1) * mm});
            skLineSegment(sketch, "E419", {"start": v(-9.41, 13.1) * mm, "end": v(-9.4, 6.7) * mm});
            skLineSegment(sketch, "E420", {"start": v(-9.4, 6.7) * mm, "end": v(-9.39, 6.05) * mm});
            skLineSegment(sketch, "E421", {"start": v(-9.39, 6.05) * mm, "end": v(-9.39, 5.9) * mm});
            skLineSegment(sketch, "E422", {"start": v(-9.39, 5.9) * mm, "end": v(-9.36, 4.33) * mm});
            skLineSegment(sketch, "E423", {"start": v(-9.36, 4.33) * mm, "end": v(-9.34, 4.18) * mm});
            skLineSegment(sketch, "E424", {"start": v(-9.34, 4.18) * mm, "end": v(-9.02, 4.18) * mm});
            skLineSegment(sketch, "E425", {"start": v(-9.02, 4.18) * mm, "end": v(-5.82, 4.14) * mm});
            skLineSegment(sketch, "E426", {"start": v(-5.82, 4.14) * mm, "end": v(-5.5, 4.16) * mm});
            skLineSegment(sketch, "E427", {"start": v(-5.5, 4.16) * mm, "end": v(-5.48, 4.98) * mm});
            skLineSegment(sketch, "E428", {"start": v(-5.48, 4.98) * mm, "end": v(-5.45, 13.17) * mm});
            skLineSegment(sketch, "E429", {"start": v(-5.45, 13.17) * mm, "end": v(-5.45, 13.99) * mm});
            skLineSegment(sketch, "E430", {"start": v(-5.45, 13.99) * mm, "end": v(-5.45, 14.13) * mm});
            skLineSegment(sketch, "E431", {"start": v(-5.45, 14.13) * mm, "end": v(-5.42, 15.61) * mm});
            skLineSegment(sketch, "E432", {"start": v(-5.42, 15.61) * mm, "end": v(-5.4, 15.76) * mm});
            skLineSegment(sketch, "E433", {"start": v(5.48, 9.66) * mm, "end": v(5.66, 9.66) * mm});
            skLineSegment(sketch, "E434", {"start": v(5.66, 9.66) * mm, "end": v(6.56, 9.47) * mm});
            skLineSegment(sketch, "E435", {"start": v(6.56, 9.47) * mm, "end": v(7.4, 9.1) * mm});
            skLineSegment(sketch, "E436", {"start": v(7.4, 9.1) * mm, "end": v(7.57, 9.02) * mm});
            skLineSegment(sketch, "E437", {"start": v(7.57, 9.02) * mm, "end": v(7.75, 8.92) * mm});
            skLineSegment(sketch, "E438", {"start": v(7.75, 8.92) * mm, "end": v(8.23, 8.53) * mm});
            skLineSegment(sketch, "E439", {"start": v(8.23, 8.53) * mm, "end": v(8.74, 7.89) * mm});
            skLineSegment(sketch, "E440", {"start": v(8.74, 7.89) * mm, "end": v(9.09, 7.14) * mm});
            skLineSegment(sketch, "E441", {"start": v(9.09, 7.14) * mm, "end": v(9.24, 6.54) * mm});
            skLineSegment(sketch, "E442", {"start": v(9.24, 6.54) * mm, "end": v(9.26, 6.34) * mm});
            skLineSegment(sketch, "E443", {"start": v(9.26, 6.34) * mm, "end": v(9.27, 6.16) * mm});
            skLineSegment(sketch, "E444", {"start": v(9.27, 6.16) * mm, "end": v(9.25, 5.25) * mm});
            skLineSegment(sketch, "E445", {"start": v(9.25, 5.25) * mm, "end": v(9.02, 4.38) * mm});
            skLineSegment(sketch, "E446", {"start": v(9.02, 4.38) * mm, "end": v(8.94, 4.22) * mm});
            skLineSegment(sketch, "E447", {"start": v(8.94, 4.22) * mm, "end": v(8.88, 4.11) * mm});
            skLineSegment(sketch, "E448", {"start": v(8.88, 4.11) * mm, "end": v(8.56, 3.6) * mm});
            skLineSegment(sketch, "E449", {"start": v(8.56, 3.6) * mm, "end": v(8.17, 3.13) * mm});
            skLineSegment(sketch, "E450", {"start": v(8.17, 3.13) * mm, "end": v(8.08, 3.05) * mm});
            skLineSegment(sketch, "E451", {"start": v(8.08, 3.05) * mm, "end": v(7.94, 2.94) * mm});
            skLineSegment(sketch, "E452", {"start": v(7.94, 2.94) * mm, "end": v(7.48, 2.64) * mm});
            skLineSegment(sketch, "E453", {"start": v(7.48, 2.64) * mm, "end": v(6.82, 2.33) * mm});
            skLineSegment(sketch, "E454", {"start": v(6.82, 2.33) * mm, "end": v(6.13, 2.12) * mm});
            skLineSegment(sketch, "E455", {"start": v(6.13, 2.12) * mm, "end": v(5.58, 2.05) * mm});
            skLineSegment(sketch, "E456", {"start": v(5.58, 2.05) * mm, "end": v(5.4, 2.05) * mm});
            skLineSegment(sketch, "E457", {"start": v(5.4, 2.05) * mm, "end": v(5.4, 2.27) * mm});
            skLineSegment(sketch, "E458", {"start": v(5.4, 2.27) * mm, "end": v(5.4, 4.48) * mm});
            skLineSegment(sketch, "E459", {"start": v(5.4, 4.48) * mm, "end": v(5.42, 4.7) * mm});
            skLineSegment(sketch, "E460", {"start": v(5.42, 4.7) * mm, "end": v(5.43, 5.11) * mm});
            skLineSegment(sketch, "E461", {"start": v(5.43, 5.11) * mm, "end": v(5.47, 9.25) * mm});
            skLineSegment(sketch, "E462", {"start": v(5.47, 9.25) * mm, "end": v(5.48, 9.66) * mm});
            skLineSegment(sketch, "E463", {"start": v(5.5, -2.06) * mm, "end": v(5.68, -2.07) * mm});
            skLineSegment(sketch, "E464", {"start": v(5.68, -2.07) * mm, "end": v(6.22, -2.17) * mm});
            skLineSegment(sketch, "E465", {"start": v(6.22, -2.17) * mm, "end": v(6.91, -2.4) * mm});
            skLineSegment(sketch, "E466", {"start": v(6.91, -2.4) * mm, "end": v(7.55, -2.74) * mm});
            skLineSegment(sketch, "E467", {"start": v(7.55, -2.74) * mm, "end": v(7.98, -3.09) * mm});
            skLineSegment(sketch, "E468", {"start": v(7.98, -3.09) * mm, "end": v(8.1, -3.22) * mm});
            skLineSegment(sketch, "E469", {"start": v(8.1, -3.22) * mm, "end": v(8.24, -3.37) * mm});
            skLineSegment(sketch, "E470", {"start": v(8.24, -3.37) * mm, "end": v(8.6, -3.85) * mm});
            skLineSegment(sketch, "E471", {"start": v(8.6, -3.85) * mm, "end": v(8.93, -4.57) * mm});
            skLineSegment(sketch, "E472", {"start": v(8.93, -4.57) * mm, "end": v(9.13, -5.35) * mm});
            skLineSegment(sketch, "E473", {"start": v(9.13, -5.35) * mm, "end": v(9.19, -5.95) * mm});
            skLineSegment(sketch, "E474", {"start": v(9.19, -5.95) * mm, "end": v(9.18, -6.15) * mm});
            skLineSegment(sketch, "E475", {"start": v(9.18, -6.15) * mm, "end": v(9.18, -6.33) * mm});
            skLineSegment(sketch, "E476", {"start": v(9.18, -6.33) * mm, "end": v(9.08, -6.87) * mm});
            skLineSegment(sketch, "E477", {"start": v(9.08, -6.87) * mm, "end": v(8.8, -7.54) * mm});
            skLineSegment(sketch, "E478", {"start": v(8.8, -7.54) * mm, "end": v(8.4, -8.15) * mm});
            skLineSegment(sketch, "E479", {"start": v(8.4, -8.15) * mm, "end": v(8.06, -8.57) * mm});
            skLineSegment(sketch, "E480", {"start": v(8.06, -8.57) * mm, "end": v(7.93, -8.7) * mm});
            skLineSegment(sketch, "E481", {"start": v(7.93, -8.7) * mm, "end": v(7.8, -8.82) * mm});
            skLineSegment(sketch, "E482", {"start": v(7.8, -8.82) * mm, "end": v(7.4, -9.1) * mm});
            skLineSegment(sketch, "E483", {"start": v(7.4, -9.1) * mm, "end": v(6.8, -9.4) * mm});
            skLineSegment(sketch, "E484", {"start": v(6.8, -9.4) * mm, "end": v(6.15, -9.57) * mm});
            skLineSegment(sketch, "E485", {"start": v(6.15, -9.57) * mm, "end": v(5.65, -9.63) * mm});
            skLineSegment(sketch, "E486", {"start": v(5.65, -9.63) * mm, "end": v(5.48, -9.62) * mm});
            skLineSegment(sketch, "E487", {"start": v(5.48, -9.62) * mm, "end": v(5.47, -9) * mm});
            skLineSegment(sketch, "E488", {"start": v(5.47, -9) * mm, "end": v(5.5, -2.69) * mm});
            skLineSegment(sketch, "E489", {"start": v(5.5, -2.69) * mm, "end": v(5.5, -2.06) * mm});
            skLineSegment(sketch, "E490", {"start": v(-10.95, -16.44) * mm, "end": v(-10.78, -16.4) * mm});
            skLineSegment(sketch, "E491", {"start": v(-10.78, -16.4) * mm, "end": v(-10.25, -16.35) * mm});
            skLineSegment(sketch, "E492", {"start": v(-10.25, -16.35) * mm, "end": v(-9.56, -16.45) * mm});
            skLineSegment(sketch, "E493", {"start": v(-9.56, -16.45) * mm, "end": v(-8.91, -16.73) * mm});
            skLineSegment(sketch, "E494", {"start": v(-8.91, -16.73) * mm, "end": v(-8.48, -17.04) * mm});
            skLineSegment(sketch, "E495", {"start": v(-8.48, -17.04) * mm, "end": v(-8.37, -17.17) * mm});
            skLineSegment(sketch, "E496", {"start": v(-8.37, -17.17) * mm, "end": v(-8.3, -17.28) * mm});
            skLineSegment(sketch, "E497", {"start": v(-8.3, -17.28) * mm, "end": v(-8.1, -17.64) * mm});
            skLineSegment(sketch, "E498", {"start": v(-8.1, -17.64) * mm, "end": v(-7.9, -18.15) * mm});
            skLineSegment(sketch, "E499", {"start": v(-7.9, -18.15) * mm, "end": v(-7.81, -18.68) * mm});
            skLineSegment(sketch, "E500", {"start": v(-7.81, -18.68) * mm, "end": v(-7.83, -19.1) * mm});
            skLineSegment(sketch, "E501", {"start": v(-7.83, -19.1) * mm, "end": v(-7.86, -19.22) * mm});
            skLineSegment(sketch, "E502", {"start": v(-7.86, -19.22) * mm, "end": v(-7.9, -19.3) * mm});
            skLineSegment(sketch, "E503", {"start": v(-7.9, -19.3) * mm, "end": v(-7.97, -19.55) * mm});
            skLineSegment(sketch, "E504", {"start": v(-7.97, -19.55) * mm, "end": v(-8.1, -19.88) * mm});
            skLineSegment(sketch, "E505", {"start": v(-8.1, -19.88) * mm, "end": v(-8.27, -20.18) * mm});
            skLineSegment(sketch, "E506", {"start": v(-8.27, -20.18) * mm, "end": v(-8.44, -20.37) * mm});
            skLineSegment(sketch, "E507", {"start": v(-8.44, -20.37) * mm, "end": v(-8.51, -20.42) * mm});
            skLineSegment(sketch, "E508", {"start": v(-8.51, -20.42) * mm, "end": v(-8.62, -20.5) * mm});
            skLineSegment(sketch, "E509", {"start": v(-8.62, -20.5) * mm, "end": v(-9.24, -20.85) * mm});
            skLineSegment(sketch, "E510", {"start": v(-9.24, -20.85) * mm, "end": v(-9.9, -21.07) * mm});
            skLineSegment(sketch, "E511", {"start": v(-9.9, -21.07) * mm, "end": v(-10.04, -21.1) * mm});
            skLineSegment(sketch, "E512", {"start": v(-10.04, -21.1) * mm, "end": v(-10.13, -21.1) * mm});
            skLineSegment(sketch, "E513", {"start": v(-10.13, -21.1) * mm, "end": v(-10.6, -21.05) * mm});
            skLineSegment(sketch, "E514", {"start": v(-10.6, -21.05) * mm, "end": v(-11.05, -20.94) * mm});
            skLineSegment(sketch, "E515", {"start": v(-11.05, -20.94) * mm, "end": v(-11.14, -20.91) * mm});
            skLineSegment(sketch, "E516", {"start": v(-11.14, -20.91) * mm, "end": v(-11.22, -20.88) * mm});
            skLineSegment(sketch, "E517", {"start": v(-11.22, -20.88) * mm, "end": v(-11.59, -20.64) * mm});
            skLineSegment(sketch, "E518", {"start": v(-11.59, -20.64) * mm, "end": v(-11.94, -20.38) * mm});
            skLineSegment(sketch, "E519", {"start": v(-11.94, -20.38) * mm, "end": v(-12, -20.33) * mm});
            skLineSegment(sketch, "E520", {"start": v(-12, -20.33) * mm, "end": v(-12.11, -20.23) * mm});
            skLineSegment(sketch, "E521", {"start": v(-12.11, -20.23) * mm, "end": v(-12.38, -19.88) * mm});
            skLineSegment(sketch, "E522", {"start": v(-12.38, -19.88) * mm, "end": v(-12.6, -19.35) * mm});
            skLineSegment(sketch, "E523", {"start": v(-12.6, -19.35) * mm, "end": v(-12.7, -18.77) * mm});
            skLineSegment(sketch, "E524", {"start": v(-12.7, -18.77) * mm, "end": v(-12.69, -18.34) * mm});
            skLineSegment(sketch, "E525", {"start": v(-12.69, -18.34) * mm, "end": v(-12.66, -18.2) * mm});
            skLineSegment(sketch, "E526", {"start": v(-12.66, -18.2) * mm, "end": v(-12.62, -18.07) * mm});
            skLineSegment(sketch, "E527", {"start": v(-12.62, -18.07) * mm, "end": v(-12.33, -17.5) * mm});
            skLineSegment(sketch, "E528", {"start": v(-12.33, -17.5) * mm, "end": v(-11.95, -16.97) * mm});
            skLineSegment(sketch, "E529", {"start": v(-11.95, -16.97) * mm, "end": v(-11.86, -16.87) * mm});
            skLineSegment(sketch, "E530", {"start": v(-11.86, -16.87) * mm, "end": v(-11.82, -16.83) * mm});
            skLineSegment(sketch, "E531", {"start": v(-11.82, -16.83) * mm, "end": v(-11.66, -16.72) * mm});
            skLineSegment(sketch, "E532", {"start": v(-11.66, -16.72) * mm, "end": v(-11.43, -16.6) * mm});
            skLineSegment(sketch, "E533", {"start": v(-11.43, -16.6) * mm, "end": v(-11.2, -16.52) * mm});
            skLineSegment(sketch, "E534", {"start": v(-11.2, -16.52) * mm, "end": v(-11, -16.46) * mm});
            skLineSegment(sketch, "E535", {"start": v(-11, -16.46) * mm, "end": v(-10.95, -16.44) * mm});
            skLineSegment(sketch, "E536", {"start": v(8.92, -16.87) * mm, "end": v(9, -16.81) * mm});
            skLineSegment(sketch, "E537", {"start": v(9, -16.81) * mm, "end": v(9.27, -16.67) * mm});
            skLineSegment(sketch, "E538", {"start": v(9.27, -16.67) * mm, "end": v(9.63, -16.52) * mm});
            skLineSegment(sketch, "E539", {"start": v(9.63, -16.52) * mm, "end": v(10, -16.42) * mm});
            skLineSegment(sketch, "E540", {"start": v(10, -16.42) * mm, "end": v(10.3, -16.4) * mm});
            skLineSegment(sketch, "E541", {"start": v(10.3, -16.4) * mm, "end": v(10.4, -16.4) * mm});
            skLineSegment(sketch, "E542", {"start": v(10.4, -16.4) * mm, "end": v(10.49, -16.4) * mm});
            skLineSegment(sketch, "E543", {"start": v(10.49, -16.4) * mm, "end": v(10.75, -16.49) * mm});
            skLineSegment(sketch, "E544", {"start": v(10.75, -16.49) * mm, "end": v(11.03, -16.7) * mm});
            skLineSegment(sketch, "E545", {"start": v(11.03, -16.7) * mm, "end": v(11.23, -17) * mm});
            skLineSegment(sketch, "E546", {"start": v(11.23, -17) * mm, "end": v(11.32, -17.24) * mm});
            skLineSegment(sketch, "E547", {"start": v(11.32, -17.24) * mm, "end": v(11.33, -17.33) * mm});
            skLineSegment(sketch, "E548", {"start": v(11.33, -17.33) * mm, "end": v(11.35, -17.39) * mm});
            skLineSegment(sketch, "E549", {"start": v(11.35, -17.39) * mm, "end": v(11.34, -17.59) * mm});
            skLineSegment(sketch, "E550", {"start": v(11.34, -17.59) * mm, "end": v(11.27, -17.84) * mm});
            skLineSegment(sketch, "E551", {"start": v(11.27, -17.84) * mm, "end": v(11.16, -18.08) * mm});
            skLineSegment(sketch, "E552", {"start": v(11.16, -18.08) * mm, "end": v(11.08, -18.26) * mm});
            skLineSegment(sketch, "E553", {"start": v(11.08, -18.26) * mm, "end": v(11.05, -18.32) * mm});
            skLineSegment(sketch, "E554", {"start": v(11.05, -18.32) * mm, "end": v(11.21, -18.4) * mm});
            skLineSegment(sketch, "E555", {"start": v(11.21, -18.4) * mm, "end": v(12.03, -18.78) * mm});
            skLineSegment(sketch, "E556", {"start": v(12.03, -18.78) * mm, "end": v(12.87, -19.1) * mm});
            skLineSegment(sketch, "E557", {"start": v(12.87, -19.1) * mm, "end": v(13.05, -19.14) * mm});
            skLineSegment(sketch, "E558", {"start": v(13.05, -19.14) * mm, "end": v(13.13, -19.16) * mm});
            skLineSegment(sketch, "E559", {"start": v(13.13, -19.16) * mm, "end": v(13.96, -19.25) * mm});
            skLineSegment(sketch, "E560", {"start": v(13.96, -19.25) * mm, "end": v(14.04, -19.27) * mm});
            skLineSegment(sketch, "E561", {"start": v(14.04, -19.27) * mm, "end": v(13.95, -19.34) * mm});
            skLineSegment(sketch, "E562", {"start": v(13.95, -19.34) * mm, "end": v(13.67, -19.53) * mm});
            skLineSegment(sketch, "E563", {"start": v(13.67, -19.53) * mm, "end": v(13.27, -19.74) * mm});
            skLineSegment(sketch, "E564", {"start": v(13.27, -19.74) * mm, "end": v(12.84, -19.83) * mm});
            skLineSegment(sketch, "E565", {"start": v(12.84, -19.83) * mm, "end": v(12.5, -19.79) * mm});
            skLineSegment(sketch, "E566", {"start": v(12.5, -19.79) * mm, "end": v(12.4, -19.74) * mm});
            skLineSegment(sketch, "E567", {"start": v(12.4, -19.74) * mm, "end": v(12.24, -19.67) * mm});
            skLineSegment(sketch, "E568", {"start": v(12.24, -19.67) * mm, "end": v(11.5, -19.28) * mm});
            skLineSegment(sketch, "E569", {"start": v(11.5, -19.28) * mm, "end": v(10.75, -18.95) * mm});
            skLineSegment(sketch, "E570", {"start": v(10.75, -18.95) * mm, "end": v(10.58, -18.91) * mm});
            skLineSegment(sketch, "E571", {"start": v(10.58, -18.91) * mm, "end": v(10.53, -18.9) * mm});
            skLineSegment(sketch, "E572", {"start": v(10.53, -18.9) * mm, "end": v(10.38, -18.9) * mm});
            skLineSegment(sketch, "E573", {"start": v(10.38, -18.9) * mm, "end": v(10.17, -18.93) * mm});
            skLineSegment(sketch, "E574", {"start": v(10.17, -18.93) * mm, "end": v(10, -19.03) * mm});
            skLineSegment(sketch, "E575", {"start": v(10, -19.03) * mm, "end": v(9.9, -19.16) * mm});
            skLineSegment(sketch, "E576", {"start": v(9.9, -19.16) * mm, "end": v(9.9, -19.2) * mm});
            skLineSegment(sketch, "E577", {"start": v(9.9, -19.2) * mm, "end": v(9.95, -19.32) * mm});
            skLineSegment(sketch, "E578", {"start": v(9.95, -19.32) * mm, "end": v(10.23, -19.9) * mm});
            skLineSegment(sketch, "E579", {"start": v(10.23, -19.9) * mm, "end": v(10.57, -20.44) * mm});
            skLineSegment(sketch, "E580", {"start": v(10.57, -20.44) * mm, "end": v(10.64, -20.54) * mm});
            skLineSegment(sketch, "E581", {"start": v(10.64, -20.54) * mm, "end": v(10.7, -20.56) * mm});
            skLineSegment(sketch, "E582", {"start": v(10.7, -20.56) * mm, "end": v(10.9, -20.56) * mm});
            skLineSegment(sketch, "E583", {"start": v(10.9, -20.56) * mm, "end": v(11.15, -20.5) * mm});
            skLineSegment(sketch, "E584", {"start": v(11.15, -20.5) * mm, "end": v(11.4, -20.43) * mm});
            skLineSegment(sketch, "E585", {"start": v(11.4, -20.43) * mm, "end": v(11.58, -20.37) * mm});
            skLineSegment(sketch, "E586", {"start": v(11.58, -20.37) * mm, "end": v(11.65, -20.35) * mm});
            skLineSegment(sketch, "E587", {"start": v(11.65, -20.35) * mm, "end": v(11.64, -20.38) * mm});
            skLineSegment(sketch, "E588", {"start": v(11.64, -20.38) * mm, "end": v(11.6, -20.67) * mm});
            skLineSegment(sketch, "E589", {"start": v(11.6, -20.67) * mm, "end": v(11.6, -20.7) * mm});
            skLineSegment(sketch, "E590", {"start": v(11.6, -20.7) * mm, "end": v(11.5, -20.74) * mm});
            skLineSegment(sketch, "E591", {"start": v(11.5, -20.74) * mm, "end": v(10.96, -20.91) * mm});
            skLineSegment(sketch, "E592", {"start": v(10.96, -20.91) * mm, "end": v(10.46, -21.14) * mm});
            skLineSegment(sketch, "E593", {"start": v(10.46, -21.14) * mm, "end": v(10.36, -21.2) * mm});
            skLineSegment(sketch, "E594", {"start": v(10.36, -21.2) * mm, "end": v(10.3, -21.24) * mm});
            skLineSegment(sketch, "E595", {"start": v(10.3, -21.24) * mm, "end": v(9.69, -21.57) * mm});
            skLineSegment(sketch, "E596", {"start": v(9.69, -21.57) * mm, "end": v(9.63, -21.6) * mm});
            skLineSegment(sketch, "E597", {"start": v(9.63, -21.6) * mm, "end": v(9.66, -21.54) * mm});
            skLineSegment(sketch, "E598", {"start": v(9.66, -21.54) * mm, "end": v(9.83, -21.28) * mm});
            skLineSegment(sketch, "E599", {"start": v(9.83, -21.28) * mm, "end": v(9.98, -21.02) * mm});
            skLineSegment(sketch, "E600", {"start": v(9.98, -21.02) * mm, "end": v(10, -20.96) * mm});
            skLineSegment(sketch, "E601", {"start": v(10, -20.96) * mm, "end": v(10, -20.9) * mm});
            skLineSegment(sketch, "E602", {"start": v(10, -20.9) * mm, "end": v(9.95, -20.69) * mm});
            skLineSegment(sketch, "E603", {"start": v(9.95, -20.69) * mm, "end": v(9.85, -20.43) * mm});
            skLineSegment(sketch, "E604", {"start": v(9.85, -20.43) * mm, "end": v(9.72, -20.19) * mm});
            skLineSegment(sketch, "E605", {"start": v(9.72, -20.19) * mm, "end": v(9.62, -20) * mm});
            skLineSegment(sketch, "E606", {"start": v(9.62, -20) * mm, "end": v(9.58, -19.94) * mm});
            skLineSegment(sketch, "E607", {"start": v(9.58, -19.94) * mm, "end": v(9.53, -19.85) * mm});
            skLineSegment(sketch, "E608", {"start": v(9.53, -19.85) * mm, "end": v(9.27, -19.38) * mm});
            skLineSegment(sketch, "E609", {"start": v(9.27, -19.38) * mm, "end": v(9, -18.91) * mm});
            skLineSegment(sketch, "E610", {"start": v(9, -18.91) * mm, "end": v(8.96, -18.82) * mm});
            skLineSegment(sketch, "E611", {"start": v(8.96, -18.82) * mm, "end": v(8.93, -18.75) * mm});
            skLineSegment(sketch, "E612", {"start": v(8.93, -18.75) * mm, "end": v(8.83, -18.55) * mm});
            skLineSegment(sketch, "E613", {"start": v(8.83, -18.55) * mm, "end": v(8.69, -18.28) * mm});
            skLineSegment(sketch, "E614", {"start": v(8.69, -18.28) * mm, "end": v(8.52, -18.04) * mm});
            skLineSegment(sketch, "E615", {"start": v(8.52, -18.04) * mm, "end": v(8.38, -17.87) * mm});
            skLineSegment(sketch, "E616", {"start": v(8.38, -17.87) * mm, "end": v(8.32, -17.82) * mm});
            skLineSegment(sketch, "E617", {"start": v(8.32, -17.82) * mm, "end": v(8.26, -17.8) * mm});
            skLineSegment(sketch, "E618", {"start": v(8.26, -17.8) * mm, "end": v(7.92, -17.75) * mm});
            skLineSegment(sketch, "E619", {"start": v(7.92, -17.75) * mm, "end": v(7.58, -17.72) * mm});
            skLineSegment(sketch, "E620", {"start": v(7.58, -17.72) * mm, "end": v(7.51, -17.71) * mm});
            skLineSegment(sketch, "E621", {"start": v(7.51, -17.71) * mm, "end": v(7.6, -17.65) * mm});
            skLineSegment(sketch, "E622", {"start": v(7.6, -17.65) * mm, "end": v(7.85, -17.47) * mm});
            skLineSegment(sketch, "E623", {"start": v(7.85, -17.47) * mm, "end": v(8.2, -17.26) * mm});
            skLineSegment(sketch, "E624", {"start": v(8.2, -17.26) * mm, "end": v(8.57, -17.07) * mm});
            skLineSegment(sketch, "E625", {"start": v(8.57, -17.07) * mm, "end": v(8.84, -16.92) * mm});
            skLineSegment(sketch, "E626", {"start": v(8.84, -16.92) * mm, "end": v(8.92, -16.87) * mm});
            skLineSegment(sketch, "E627", {"start": v(-10.27, -16.62) * mm, "end": v(-10.2, -16.6) * mm});
            skLineSegment(sketch, "E628", {"start": v(-10.2, -16.6) * mm, "end": v(-9.98, -16.59) * mm});
            skLineSegment(sketch, "E629", {"start": v(-9.98, -16.59) * mm, "end": v(-9.69, -16.62) * mm});
            skLineSegment(sketch, "E630", {"start": v(-9.69, -16.62) * mm, "end": v(-9.41, -16.73) * mm});
            skLineSegment(sketch, "E631", {"start": v(-9.41, -16.73) * mm, "end": v(-9.23, -16.86) * mm});
            skLineSegment(sketch, "E632", {"start": v(-9.23, -16.86) * mm, "end": v(-9.19, -16.92) * mm});
            skLineSegment(sketch, "E633", {"start": v(-9.19, -16.92) * mm, "end": v(-9.14, -16.97) * mm});
            skLineSegment(sketch, "E634", {"start": v(-9.14, -16.97) * mm, "end": v(-9, -17.12) * mm});
            skLineSegment(sketch, "E635", {"start": v(-9, -17.12) * mm, "end": v(-8.84, -17.33) * mm});
            skLineSegment(sketch, "E636", {"start": v(-8.84, -17.33) * mm, "end": v(-8.7, -17.55) * mm});
            skLineSegment(sketch, "E637", {"start": v(-8.7, -17.55) * mm, "end": v(-8.61, -17.74) * mm});
            skLineSegment(sketch, "E638", {"start": v(-8.61, -17.74) * mm, "end": v(-8.6, -17.8) * mm});
            skLineSegment(sketch, "E639", {"start": v(-8.6, -17.8) * mm, "end": v(-8.57, -17.88) * mm});
            skLineSegment(sketch, "E640", {"start": v(-8.57, -17.88) * mm, "end": v(-8.55, -18.13) * mm});
            skLineSegment(sketch, "E641", {"start": v(-8.55, -18.13) * mm, "end": v(-8.56, -18.46) * mm});
            skLineSegment(sketch, "E642", {"start": v(-8.56, -18.46) * mm, "end": v(-8.61, -18.79) * mm});
            skLineSegment(sketch, "E643", {"start": v(-8.61, -18.79) * mm, "end": v(-8.66, -19.03) * mm});
            skLineSegment(sketch, "E644", {"start": v(-8.66, -19.03) * mm, "end": v(-8.67, -19.12) * mm});
            skLineSegment(sketch, "E645", {"start": v(-8.67, -19.12) * mm, "end": v(-8.69, -19.24) * mm});
            skLineSegment(sketch, "E646", {"start": v(-8.69, -19.24) * mm, "end": v(-8.82, -19.59) * mm});
            skLineSegment(sketch, "E647", {"start": v(-8.82, -19.59) * mm, "end": v(-9.09, -20) * mm});
            skLineSegment(sketch, "E648", {"start": v(-9.09, -20) * mm, "end": v(-9.44, -20.35) * mm});
            skLineSegment(sketch, "E649", {"start": v(-9.44, -20.35) * mm, "end": v(-9.75, -20.56) * mm});
            skLineSegment(sketch, "E650", {"start": v(-9.75, -20.56) * mm, "end": v(-9.86, -20.62) * mm});
            skLineSegment(sketch, "E651", {"start": v(-9.86, -20.62) * mm, "end": v(-9.94, -20.66) * mm});
            skLineSegment(sketch, "E652", {"start": v(-9.94, -20.66) * mm, "end": v(-10.21, -20.73) * mm});
            skLineSegment(sketch, "E653", {"start": v(-10.21, -20.73) * mm, "end": v(-10.58, -20.71) * mm});
            skLineSegment(sketch, "E654", {"start": v(-10.58, -20.71) * mm, "end": v(-10.94, -20.62) * mm});
            skLineSegment(sketch, "E655", {"start": v(-10.94, -20.62) * mm, "end": v(-11.2, -20.52) * mm});
            skLineSegment(sketch, "E656", {"start": v(-11.2, -20.52) * mm, "end": v(-11.28, -20.48) * mm});
            skLineSegment(sketch, "E657", {"start": v(-11.28, -20.48) * mm, "end": v(-11.35, -20.43) * mm});
            skLineSegment(sketch, "E658", {"start": v(-11.35, -20.43) * mm, "end": v(-11.53, -20.27) * mm});
            skLineSegment(sketch, "E659", {"start": v(-11.53, -20.27) * mm, "end": v(-11.73, -20.01) * mm});
            skLineSegment(sketch, "E660", {"start": v(-11.73, -20.01) * mm, "end": v(-11.87, -19.71) * mm});
            skLineSegment(sketch, "E661", {"start": v(-11.87, -19.71) * mm, "end": v(-11.94, -19.48) * mm});
            skLineSegment(sketch, "E662", {"start": v(-11.94, -19.48) * mm, "end": v(-11.95, -19.4) * mm});
            skLineSegment(sketch, "E663", {"start": v(-11.95, -19.4) * mm, "end": v(-11.96, -19.24) * mm});
            skLineSegment(sketch, "E664", {"start": v(-11.96, -19.24) * mm, "end": v(-11.94, -18.75) * mm});
            skLineSegment(sketch, "E665", {"start": v(-11.94, -18.75) * mm, "end": v(-11.81, -18.1) * mm});
            skLineSegment(sketch, "E666", {"start": v(-11.81, -18.1) * mm, "end": v(-11.56, -17.51) * mm});
            skLineSegment(sketch, "E667", {"start": v(-11.56, -17.51) * mm, "end": v(-11.29, -17.1) * mm});
            skLineSegment(sketch, "E668", {"start": v(-11.29, -17.1) * mm, "end": v(-11.17, -16.99) * mm});
            skLineSegment(sketch, "E669", {"start": v(-11.17, -16.99) * mm, "end": v(-11.13, -16.94) * mm});
            skLineSegment(sketch, "E670", {"start": v(-11.13, -16.94) * mm, "end": v(-10.98, -16.83) * mm});
            skLineSegment(sketch, "E671", {"start": v(-10.98, -16.83) * mm, "end": v(-10.75, -16.73) * mm});
            skLineSegment(sketch, "E672", {"start": v(-10.75, -16.73) * mm, "end": v(-10.52, -16.67) * mm});
            skLineSegment(sketch, "E673", {"start": v(-10.52, -16.67) * mm, "end": v(-10.33, -16.63) * mm});
            skLineSegment(sketch, "E674", {"start": v(-10.33, -16.63) * mm, "end": v(-10.27, -16.62) * mm});
            skLineSegment(sketch, "E675", {"start": v(8.93, -17.28) * mm, "end": v(8.96, -17.24) * mm});
            skLineSegment(sketch, "E676", {"start": v(8.96, -17.24) * mm, "end": v(9.07, -17.12) * mm});
            skLineSegment(sketch, "E677", {"start": v(9.07, -17.12) * mm, "end": v(9.26, -17) * mm});
            skLineSegment(sketch, "E678", {"start": v(9.26, -17) * mm, "end": v(9.47, -16.9) * mm});
            skLineSegment(sketch, "E679", {"start": v(9.47, -16.9) * mm, "end": v(9.69, -16.87) * mm});
            skLineSegment(sketch, "E680", {"start": v(9.69, -16.87) * mm, "end": v(9.9, -16.88) * mm});
            skLineSegment(sketch, "E681", {"start": v(9.9, -16.88) * mm, "end": v(10.12, -16.94) * mm});
            skLineSegment(sketch, "E682", {"start": v(10.12, -16.94) * mm, "end": v(10.3, -17.05) * mm});
            skLineSegment(sketch, "E683", {"start": v(10.3, -17.05) * mm, "end": v(10.43, -17.17) * mm});
            skLineSegment(sketch, "E684", {"start": v(10.43, -17.17) * mm, "end": v(10.46, -17.22) * mm});
            skLineSegment(sketch, "E685", {"start": v(10.46, -17.22) * mm, "end": v(10.5, -17.28) * mm});
            skLineSegment(sketch, "E686", {"start": v(10.5, -17.28) * mm, "end": v(10.61, -17.48) * mm});
            skLineSegment(sketch, "E687", {"start": v(10.61, -17.48) * mm, "end": v(10.68, -17.78) * mm});
            skLineSegment(sketch, "E688", {"start": v(10.68, -17.78) * mm, "end": v(10.64, -18.07) * mm});
            skLineSegment(sketch, "E689", {"start": v(10.64, -18.07) * mm, "end": v(10.54, -18.28) * mm});
            skLineSegment(sketch, "E690", {"start": v(10.54, -18.28) * mm, "end": v(10.5, -18.34) * mm});
            skLineSegment(sketch, "E691", {"start": v(10.5, -18.34) * mm, "end": v(10.45, -18.39) * mm});
            skLineSegment(sketch, "E692", {"start": v(10.45, -18.39) * mm, "end": v(10.33, -18.54) * mm});
            skLineSegment(sketch, "E693", {"start": v(10.33, -18.54) * mm, "end": v(10.14, -18.72) * mm});
            skLineSegment(sketch, "E694", {"start": v(10.14, -18.72) * mm, "end": v(9.93, -18.87) * mm});
            skLineSegment(sketch, "E695", {"start": v(9.93, -18.87) * mm, "end": v(9.75, -18.95) * mm});
            skLineSegment(sketch, "E696", {"start": v(9.75, -18.95) * mm, "end": v(9.68, -18.96) * mm});
            skLineSegment(sketch, "E697", {"start": v(9.68, -18.96) * mm, "end": v(9.62, -18.82) * mm});
            skLineSegment(sketch, "E698", {"start": v(9.62, -18.82) * mm, "end": v(9.25, -18.14) * mm});
            skLineSegment(sketch, "E699", {"start": v(9.25, -18.14) * mm, "end": v(8.96, -17.43) * mm});
            skLineSegment(sketch, "E700", {"start": v(8.96, -17.43) * mm, "end": v(8.93, -17.28) * mm});
            skLineSegment(sketch, "E701", {"start": v(-6.65, -18.05) * mm, "end": v(-6.5, -18.06) * mm});
            skLineSegment(sketch, "E702", {"start": v(-6.5, -18.06) * mm, "end": v(-5.84, -18.2) * mm});
            skLineSegment(sketch, "E703", {"start": v(-5.84, -18.2) * mm, "end": v(-5.19, -18.37) * mm});
            skLineSegment(sketch, "E704", {"start": v(-5.19, -18.37) * mm, "end": v(-5.05, -18.4) * mm});
            skLineSegment(sketch, "E705", {"start": v(-5.05, -18.4) * mm, "end": v(-4.95, -18.42) * mm});
            skLineSegment(sketch, "E706", {"start": v(-4.95, -18.42) * mm, "end": v(-4.63, -18.5) * mm});
            skLineSegment(sketch, "E707", {"start": v(-4.63, -18.5) * mm, "end": v(-4.21, -18.66) * mm});
            skLineSegment(sketch, "E708", {"start": v(-4.21, -18.66) * mm, "end": v(-3.84, -18.9) * mm});
            skLineSegment(sketch, "E709", {"start": v(-3.84, -18.9) * mm, "end": v(-3.6, -19.12) * mm});
            skLineSegment(sketch, "E710", {"start": v(-3.6, -19.12) * mm, "end": v(-3.54, -19.21) * mm});
            skLineSegment(sketch, "E711", {"start": v(-3.54, -19.21) * mm, "end": v(-3.5, -19.27) * mm});
            skLineSegment(sketch, "E712", {"start": v(-3.5, -19.27) * mm, "end": v(-3.4, -19.48) * mm});
            skLineSegment(sketch, "E713", {"start": v(-3.4, -19.48) * mm, "end": v(-3.37, -19.78) * mm});
            skLineSegment(sketch, "E714", {"start": v(-3.37, -19.78) * mm, "end": v(-3.43, -20.08) * mm});
            skLineSegment(sketch, "E715", {"start": v(-3.43, -20.08) * mm, "end": v(-3.51, -20.3) * mm});
            skLineSegment(sketch, "E716", {"start": v(-3.51, -20.3) * mm, "end": v(-3.55, -20.35) * mm});
            skLineSegment(sketch, "E717", {"start": v(-3.55, -20.35) * mm, "end": v(-3.58, -20.41) * mm});
            skLineSegment(sketch, "E718", {"start": v(-3.58, -20.41) * mm, "end": v(-3.73, -20.57) * mm});
            skLineSegment(sketch, "E719", {"start": v(-3.73, -20.57) * mm, "end": v(-3.96, -20.71) * mm});
            skLineSegment(sketch, "E720", {"start": v(-3.96, -20.71) * mm, "end": v(-4.22, -20.83) * mm});
            skLineSegment(sketch, "E721", {"start": v(-4.22, -20.83) * mm, "end": v(-4.4, -20.9) * mm});
            skLineSegment(sketch, "E722", {"start": v(-4.4, -20.9) * mm, "end": v(-4.47, -20.94) * mm});
            skLineSegment(sketch, "E723", {"start": v(-4.47, -20.94) * mm, "end": v(-4.4, -21.1) * mm});
            skLineSegment(sketch, "E724", {"start": v(-4.4, -21.1) * mm, "end": v(-4.07, -21.96) * mm});
            skLineSegment(sketch, "E725", {"start": v(-4.07, -21.96) * mm, "end": v(-3.67, -22.77) * mm});
            skLineSegment(sketch, "E726", {"start": v(-3.67, -22.77) * mm, "end": v(-3.56, -22.92) * mm});
            skLineSegment(sketch, "E727", {"start": v(-3.56, -22.92) * mm, "end": v(-3.52, -22.99) * mm});
            skLineSegment(sketch, "E728", {"start": v(-3.52, -22.99) * mm, "end": v(-3.26, -23.3) * mm});
            skLineSegment(sketch, "E729", {"start": v(-3.26, -23.3) * mm, "end": v(-3, -23.6) * mm});
            skLineSegment(sketch, "E730", {"start": v(-3, -23.6) * mm, "end": v(-2.96, -23.67) * mm});
            skLineSegment(sketch, "E731", {"start": v(-2.96, -23.67) * mm, "end": v(-3.07, -23.66) * mm});
            skLineSegment(sketch, "E732", {"start": v(-3.07, -23.66) * mm, "end": v(-3.4, -23.6) * mm});
            skLineSegment(sketch, "E733", {"start": v(-3.4, -23.6) * mm, "end": v(-3.84, -23.47) * mm});
            skLineSegment(sketch, "E734", {"start": v(-3.84, -23.47) * mm, "end": v(-4.22, -23.23) * mm});
            skLineSegment(sketch, "E735", {"start": v(-4.22, -23.23) * mm, "end": v(-4.44, -22.97) * mm});
            skLineSegment(sketch, "E736", {"start": v(-4.44, -22.97) * mm, "end": v(-4.48, -22.86) * mm});
            skLineSegment(sketch, "E737", {"start": v(-4.48, -22.86) * mm, "end": v(-4.54, -22.71) * mm});
            skLineSegment(sketch, "E738", {"start": v(-4.54, -22.71) * mm, "end": v(-4.8, -21.92) * mm});
            skLineSegment(sketch, "E739", {"start": v(-4.8, -21.92) * mm, "end": v(-5.14, -21.15) * mm});
            skLineSegment(sketch, "E740", {"start": v(-5.14, -21.15) * mm, "end": v(-5.23, -21.01) * mm});
            skLineSegment(sketch, "E741", {"start": v(-5.23, -21.01) * mm, "end": v(-5.26, -20.97) * mm});
            skLineSegment(sketch, "E742", {"start": v(-5.26, -20.97) * mm, "end": v(-5.37, -20.87) * mm});
            skLineSegment(sketch, "E743", {"start": v(-5.37, -20.87) * mm, "end": v(-5.54, -20.78) * mm});
            skLineSegment(sketch, "E744", {"start": v(-5.54, -20.78) * mm, "end": v(-5.73, -20.72) * mm});
            skLineSegment(sketch, "E745", {"start": v(-5.73, -20.72) * mm, "end": v(-5.87, -20.7) * mm});
            skLineSegment(sketch, "E746", {"start": v(-5.87, -20.7) * mm, "end": v(-5.92, -20.7) * mm});
            skLineSegment(sketch, "E747", {"start": v(-5.92, -20.7) * mm, "end": v(-5.96, -20.83) * mm});
            skLineSegment(sketch, "E748", {"start": v(-5.96, -20.83) * mm, "end": v(-6.3, -22.19) * mm});
            skLineSegment(sketch, "E749", {"start": v(-6.3, -22.19) * mm, "end": v(-6.32, -22.32) * mm});
            skLineSegment(sketch, "E750", {"start": v(-6.32, -22.32) * mm, "end": v(-6.25, -22.37) * mm});
            skLineSegment(sketch, "E751", {"start": v(-6.25, -22.37) * mm, "end": v(-5.54, -22.76) * mm});
            skLineSegment(sketch, "E752", {"start": v(-5.54, -22.76) * mm, "end": v(-5.47, -22.8) * mm});
            skLineSegment(sketch, "E753", {"start": v(-5.47, -22.8) * mm, "end": v(-5.48, -22.8) * mm});
            skLineSegment(sketch, "E754", {"start": v(-5.48, -22.8) * mm, "end": v(-5.58, -22.9) * mm});
            skLineSegment(sketch, "E755", {"start": v(-5.58, -22.9) * mm, "end": v(-5.67, -23.01) * mm});
            skLineSegment(sketch, "E756", {"start": v(-5.67, -23.01) * mm, "end": v(-5.69, -23.03) * mm});
            skLineSegment(sketch, "E757", {"start": v(-5.69, -23.03) * mm, "end": v(-5.84, -22.95) * mm});
            skLineSegment(sketch, "E758", {"start": v(-5.84, -22.95) * mm, "end": v(-6.63, -22.64) * mm});
            skLineSegment(sketch, "E759", {"start": v(-6.63, -22.64) * mm, "end": v(-7.46, -22.44) * mm});
            skLineSegment(sketch, "E760", {"start": v(-7.46, -22.44) * mm, "end": v(-7.63, -22.43) * mm});
            skLineSegment(sketch, "E761", {"start": v(-7.63, -22.43) * mm, "end": v(-7.64, -22.42) * mm});
            skLineSegment(sketch, "E762", {"start": v(-7.64, -22.42) * mm, "end": v(-7.7, -22.28) * mm});
            skLineSegment(sketch, "E763", {"start": v(-7.7, -22.28) * mm, "end": v(-7.72, -22.27) * mm});
            skLineSegment(sketch, "E764", {"start": v(-7.72, -22.27) * mm, "end": v(-7.66, -22.26) * mm});
            skLineSegment(sketch, "E765", {"start": v(-7.66, -22.26) * mm, "end": v(-7.1, -22.18) * mm});
            skLineSegment(sketch, "E766", {"start": v(-7.1, -22.18) * mm, "end": v(-7.04, -22.18) * mm});
            skLineSegment(sketch, "E767", {"start": v(-7.04, -22.18) * mm, "end": v(-6.98, -22.06) * mm});
            skLineSegment(sketch, "E768", {"start": v(-6.98, -22.06) * mm, "end": v(-6.74, -21.42) * mm});
            skLineSegment(sketch, "E769", {"start": v(-6.74, -21.42) * mm, "end": v(-6.58, -20.77) * mm});
            skLineSegment(sketch, "E770", {"start": v(-6.58, -20.77) * mm, "end": v(-6.54, -20.63) * mm});
            skLineSegment(sketch, "E771", {"start": v(-6.54, -20.63) * mm, "end": v(-6.51, -20.47) * mm});
            skLineSegment(sketch, "E772", {"start": v(-6.51, -20.47) * mm, "end": v(-6.28, -19.7) * mm});
            skLineSegment(sketch, "E773", {"start": v(-6.28, -19.7) * mm, "end": v(-6.1, -18.9) * mm});
            skLineSegment(sketch, "E774", {"start": v(-6.1, -18.9) * mm, "end": v(-6.1, -18.73) * mm});
            skLineSegment(sketch, "E775", {"start": v(-6.1, -18.73) * mm, "end": v(-6.12, -18.68) * mm});
            skLineSegment(sketch, "E776", {"start": v(-6.12, -18.68) * mm, "end": v(-6.2, -18.54) * mm});
            skLineSegment(sketch, "E777", {"start": v(-6.2, -18.54) * mm, "end": v(-6.35, -18.37) * mm});
            skLineSegment(sketch, "E778", {"start": v(-6.35, -18.37) * mm, "end": v(-6.5, -18.22) * mm});
            skLineSegment(sketch, "E779", {"start": v(-6.5, -18.22) * mm, "end": v(-6.61, -18.1) * mm});
            skLineSegment(sketch, "E780", {"start": v(-6.61, -18.1) * mm, "end": v(-6.65, -18.05) * mm});
            skLineSegment(sketch, "E781", {"start": v(4.91, -18.66) * mm, "end": v(5.05, -18.6) * mm});
            skLineSegment(sketch, "E782", {"start": v(5.05, -18.6) * mm, "end": v(5.76, -18.41) * mm});
            skLineSegment(sketch, "E783", {"start": v(5.76, -18.41) * mm, "end": v(6.48, -18.27) * mm});
            skLineSegment(sketch, "E784", {"start": v(6.48, -18.27) * mm, "end": v(6.63, -18.24) * mm});
            skLineSegment(sketch, "E785", {"start": v(6.63, -18.24) * mm, "end": v(6.66, -18.32) * mm});
            skLineSegment(sketch, "E786", {"start": v(6.66, -18.32) * mm, "end": v(6.97, -19.1) * mm});
            skLineSegment(sketch, "E787", {"start": v(6.97, -19.1) * mm, "end": v(7, -19.17) * mm});
            skLineSegment(sketch, "E788", {"start": v(7, -19.17) * mm, "end": v(6.93, -19.13) * mm});
            skLineSegment(sketch, "E789", {"start": v(6.93, -19.13) * mm, "end": v(6.75, -19) * mm});
            skLineSegment(sketch, "E790", {"start": v(6.75, -19) * mm, "end": v(6.5, -18.8) * mm});
            skLineSegment(sketch, "E791", {"start": v(6.5, -18.8) * mm, "end": v(6.25, -18.66) * mm});
            skLineSegment(sketch, "E792", {"start": v(6.25, -18.66) * mm, "end": v(6.03, -18.6) * mm});
            skLineSegment(sketch, "E793", {"start": v(6.03, -18.6) * mm, "end": v(5.95, -18.6) * mm});
            skLineSegment(sketch, "E794", {"start": v(5.95, -18.6) * mm, "end": v(5.86, -18.62) * mm});
            skLineSegment(sketch, "E795", {"start": v(5.86, -18.62) * mm, "end": v(5.39, -18.71) * mm});
            skLineSegment(sketch, "E796", {"start": v(5.39, -18.71) * mm, "end": v(4.93, -18.86) * mm});
            skLineSegment(sketch, "E797", {"start": v(4.93, -18.86) * mm, "end": v(4.85, -18.9) * mm});
            skLineSegment(sketch, "E798", {"start": v(4.85, -18.9) * mm, "end": v(4.86, -19) * mm});
            skLineSegment(sketch, "E799", {"start": v(4.86, -19) * mm, "end": v(5.04, -20.01) * mm});
            skLineSegment(sketch, "E800", {"start": v(5.04, -20.01) * mm, "end": v(5.06, -20.11) * mm});
            skLineSegment(sketch, "E801", {"start": v(5.06, -20.11) * mm, "end": v(5.07, -20.15) * mm});
            skLineSegment(sketch, "E802", {"start": v(5.07, -20.15) * mm, "end": v(5.1, -20.27) * mm});
            skLineSegment(sketch, "E803", {"start": v(5.1, -20.27) * mm, "end": v(5.16, -20.43) * mm});
            skLineSegment(sketch, "E804", {"start": v(5.16, -20.43) * mm, "end": v(5.26, -20.57) * mm});
            skLineSegment(sketch, "E805", {"start": v(5.26, -20.57) * mm, "end": v(5.35, -20.65) * mm});
            skLineSegment(sketch, "E806", {"start": v(5.35, -20.65) * mm, "end": v(5.39, -20.67) * mm});
            skLineSegment(sketch, "E807", {"start": v(5.39, -20.67) * mm, "end": v(5.46, -20.66) * mm});
            skLineSegment(sketch, "E808", {"start": v(5.46, -20.66) * mm, "end": v(5.67, -20.63) * mm});
            skLineSegment(sketch, "E809", {"start": v(5.67, -20.63) * mm, "end": v(5.95, -20.56) * mm});
            skLineSegment(sketch, "E810", {"start": v(5.95, -20.56) * mm, "end": v(6.2, -20.45) * mm});
            skLineSegment(sketch, "E811", {"start": v(6.2, -20.45) * mm, "end": v(6.39, -20.33) * mm});
            skLineSegment(sketch, "E812", {"start": v(6.39, -20.33) * mm, "end": v(6.44, -20.28) * mm});
            skLineSegment(sketch, "E813", {"start": v(6.44, -20.28) * mm, "end": v(6.46, -20.23) * mm});
            skLineSegment(sketch, "E814", {"start": v(6.46, -20.23) * mm, "end": v(6.54, -19.92) * mm});
            skLineSegment(sketch, "E815", {"start": v(6.54, -19.92) * mm, "end": v(6.6, -19.61) * mm});
            skLineSegment(sketch, "E816", {"start": v(6.6, -19.61) * mm, "end": v(6.62, -19.55) * mm});
            skLineSegment(sketch, "E817", {"start": v(6.62, -19.55) * mm, "end": v(6.66, -19.7) * mm});
            skLineSegment(sketch, "E818", {"start": v(6.66, -19.7) * mm, "end": v(7.04, -21.14) * mm});
            skLineSegment(sketch, "E819", {"start": v(7.04, -21.14) * mm, "end": v(7.06, -21.29) * mm});
            skLineSegment(sketch, "E820", {"start": v(7.06, -21.29) * mm, "end": v(7.02, -21.24) * mm});
            skLineSegment(sketch, "E821", {"start": v(7.02, -21.24) * mm, "end": v(6.8, -21) * mm});
            skLineSegment(sketch, "E822", {"start": v(6.8, -21) * mm, "end": v(6.57, -20.79) * mm});
            skLineSegment(sketch, "E823", {"start": v(6.57, -20.79) * mm, "end": v(6.51, -20.75) * mm});
            skLineSegment(sketch, "E824", {"start": v(6.51, -20.75) * mm, "end": v(6.42, -20.74) * mm});
            skLineSegment(sketch, "E825", {"start": v(6.42, -20.74) * mm, "end": v(5.94, -20.75) * mm});
            skLineSegment(sketch, "E826", {"start": v(5.94, -20.75) * mm, "end": v(5.48, -20.85) * mm});
            skLineSegment(sketch, "E827", {"start": v(5.48, -20.85) * mm, "end": v(5.4, -20.9) * mm});
            skLineSegment(sketch, "E828", {"start": v(5.4, -20.9) * mm, "end": v(5.38, -20.98) * mm});
            skLineSegment(sketch, "E829", {"start": v(5.38, -20.98) * mm, "end": v(5.39, -21.23) * mm});
            skLineSegment(sketch, "E830", {"start": v(5.39, -21.23) * mm, "end": v(5.46, -21.56) * mm});
            skLineSegment(sketch, "E831", {"start": v(5.46, -21.56) * mm, "end": v(5.57, -21.88) * mm});
            skLineSegment(sketch, "E832", {"start": v(5.57, -21.88) * mm, "end": v(5.66, -22.1) * mm});
            skLineSegment(sketch, "E833", {"start": v(5.66, -22.1) * mm, "end": v(5.69, -22.19) * mm});
            skLineSegment(sketch, "E834", {"start": v(5.69, -22.19) * mm, "end": v(5.7, -22.23) * mm});
            skLineSegment(sketch, "E835", {"start": v(5.7, -22.23) * mm, "end": v(5.8, -22.35) * mm});
            skLineSegment(sketch, "E836", {"start": v(5.8, -22.35) * mm, "end": v(5.95, -22.45) * mm});
            skLineSegment(sketch, "E837", {"start": v(5.95, -22.45) * mm, "end": v(6.14, -22.5) * mm});
            skLineSegment(sketch, "E838", {"start": v(6.14, -22.5) * mm, "end": v(6.3, -22.5) * mm});
            skLineSegment(sketch, "E839", {"start": v(6.3, -22.5) * mm, "end": v(6.34, -22.5) * mm});
            skLineSegment(sketch, "E840", {"start": v(6.34, -22.5) * mm, "end": v(6.42, -22.48) * mm});
            skLineSegment(sketch, "E841", {"start": v(6.42, -22.48) * mm, "end": v(6.64, -22.45) * mm});
            skLineSegment(sketch, "E842", {"start": v(6.64, -22.45) * mm, "end": v(6.95, -22.38) * mm});
            skLineSegment(sketch, "E843", {"start": v(6.95, -22.38) * mm, "end": v(7.24, -22.27) * mm});
            skLineSegment(sketch, "E844", {"start": v(7.24, -22.27) * mm, "end": v(7.44, -22.15) * mm});
            skLineSegment(sketch, "E845", {"start": v(7.44, -22.15) * mm, "end": v(7.5, -22.1) * mm});
            skLineSegment(sketch, "E846", {"start": v(7.5, -22.1) * mm, "end": v(7.56, -22.04) * mm});
            skLineSegment(sketch, "E847", {"start": v(7.56, -22.04) * mm, "end": v(7.8, -21.64) * mm});
            skLineSegment(sketch, "E848", {"start": v(7.8, -21.64) * mm, "end": v(7.98, -21.22) * mm});
            skLineSegment(sketch, "E849", {"start": v(7.98, -21.22) * mm, "end": v(8.03, -21.14) * mm});
            skLineSegment(sketch, "E850", {"start": v(8.03, -21.14) * mm, "end": v(8.04, -21.23) * mm});
            skLineSegment(sketch, "E851", {"start": v(8.04, -21.23) * mm, "end": v(8.06, -22.16) * mm});
            skLineSegment(sketch, "E852", {"start": v(8.06, -22.16) * mm, "end": v(8.06, -22.26) * mm});
            skLineSegment(sketch, "E853", {"start": v(8.06, -22.26) * mm, "end": v(7.82, -22.33) * mm});
            skLineSegment(sketch, "E854", {"start": v(7.82, -22.33) * mm, "end": v(5.48, -22.99) * mm});
            skLineSegment(sketch, "E855", {"start": v(5.48, -22.99) * mm, "end": v(5.24, -23.06) * mm});
            skLineSegment(sketch, "E856", {"start": v(5.24, -23.06) * mm, "end": v(5.18, -23.08) * mm});
            skLineSegment(sketch, "E857", {"start": v(5.18, -23.08) * mm, "end": v(5.01, -23.14) * mm});
            skLineSegment(sketch, "E858", {"start": v(5.01, -23.14) * mm, "end": v(4.78, -23.24) * mm});
            skLineSegment(sketch, "E859", {"start": v(4.78, -23.24) * mm, "end": v(4.55, -23.3) * mm});
            skLineSegment(sketch, "E860", {"start": v(4.55, -23.3) * mm, "end": v(4.37, -23.3) * mm});
            skLineSegment(sketch, "E861", {"start": v(4.37, -23.3) * mm, "end": v(4.31, -23.27) * mm});
            skLineSegment(sketch, "E862", {"start": v(4.31, -23.27) * mm, "end": v(4.3, -23.26) * mm});
            skLineSegment(sketch, "E863", {"start": v(4.3, -23.26) * mm, "end": v(4.25, -23.1) * mm});
            skLineSegment(sketch, "E864", {"start": v(4.25, -23.1) * mm, "end": v(4.25, -23.09) * mm});
            skLineSegment(sketch, "E865", {"start": v(4.25, -23.09) * mm, "end": v(4.3, -23.04) * mm});
            skLineSegment(sketch, "E866", {"start": v(4.3, -23.04) * mm, "end": v(4.62, -22.88) * mm});
            skLineSegment(sketch, "E867", {"start": v(4.62, -22.88) * mm, "end": v(4.93, -22.7) * mm});
            skLineSegment(sketch, "E868", {"start": v(4.93, -22.7) * mm, "end": v(4.98, -22.65) * mm});
            skLineSegment(sketch, "E869", {"start": v(4.98, -22.65) * mm, "end": v(5, -22.6) * mm});
            skLineSegment(sketch, "E870", {"start": v(5, -22.6) * mm, "end": v(5.02, -22.38) * mm});
            skLineSegment(sketch, "E871", {"start": v(5.02, -22.38) * mm, "end": v(4.96, -22.1) * mm});
            skLineSegment(sketch, "E872", {"start": v(4.96, -22.1) * mm, "end": v(4.87, -21.83) * mm});
            skLineSegment(sketch, "E873", {"start": v(4.87, -21.83) * mm, "end": v(4.8, -21.63) * mm});
            skLineSegment(sketch, "E874", {"start": v(4.8, -21.63) * mm, "end": v(4.78, -21.57) * mm});
            skLineSegment(sketch, "E875", {"start": v(4.78, -21.57) * mm, "end": v(4.74, -21.38) * mm});
            skLineSegment(sketch, "E876", {"start": v(4.74, -21.38) * mm, "end": v(4.52, -20.45) * mm});
            skLineSegment(sketch, "E877", {"start": v(4.52, -20.45) * mm, "end": v(4.23, -19.54) * mm});
            skLineSegment(sketch, "E878", {"start": v(4.23, -19.54) * mm, "end": v(4.15, -19.37) * mm});
            skLineSegment(sketch, "E879", {"start": v(4.15, -19.37) * mm, "end": v(4.1, -19.34) * mm});
            skLineSegment(sketch, "E880", {"start": v(4.1, -19.34) * mm, "end": v(3.92, -19.3) * mm});
            skLineSegment(sketch, "E881", {"start": v(3.92, -19.3) * mm, "end": v(3.69, -19.28) * mm});
            skLineSegment(sketch, "E882", {"start": v(3.69, -19.28) * mm, "end": v(3.45, -19.3) * mm});
            skLineSegment(sketch, "E883", {"start": v(3.45, -19.3) * mm, "end": v(3.27, -19.3) * mm});
            skLineSegment(sketch, "E884", {"start": v(3.27, -19.3) * mm, "end": v(3.22, -19.3) * mm});
            skLineSegment(sketch, "E885", {"start": v(3.22, -19.3) * mm, "end": v(3.22, -19.27) * mm});
            skLineSegment(sketch, "E886", {"start": v(3.22, -19.27) * mm, "end": v(3.23, -19.16) * mm});
            skLineSegment(sketch, "E887", {"start": v(3.23, -19.16) * mm, "end": v(3.23, -19.05) * mm});
            skLineSegment(sketch, "E888", {"start": v(3.23, -19.05) * mm, "end": v(3.24, -19.03) * mm});
            skLineSegment(sketch, "E889", {"start": v(3.24, -19.03) * mm, "end": v(3.38, -19) * mm});
            skLineSegment(sketch, "E890", {"start": v(3.38, -19) * mm, "end": v(4.08, -18.88) * mm});
            skLineSegment(sketch, "E891", {"start": v(4.08, -18.88) * mm, "end": v(4.78, -18.71) * mm});
            skLineSegment(sketch, "E892", {"start": v(4.78, -18.71) * mm, "end": v(4.91, -18.66) * mm});
            skLineSegment(sketch, "E893", {"start": v(-5.85, -20.29) * mm, "end": v(-5.83, -20.14) * mm});
            skLineSegment(sketch, "E894", {"start": v(-5.83, -20.14) * mm, "end": v(-5.63, -19.45) * mm});
            skLineSegment(sketch, "E895", {"start": v(-5.63, -19.45) * mm, "end": v(-5.36, -18.78) * mm});
            skLineSegment(sketch, "E896", {"start": v(-5.36, -18.78) * mm, "end": v(-5.3, -18.65) * mm});
            skLineSegment(sketch, "E897", {"start": v(-5.3, -18.65) * mm, "end": v(-5.24, -18.66) * mm});
            skLineSegment(sketch, "E898", {"start": v(-5.24, -18.66) * mm, "end": v(-5.06, -18.7) * mm});
            skLineSegment(sketch, "E899", {"start": v(-5.06, -18.7) * mm, "end": v(-4.82, -18.76) * mm});
            skLineSegment(sketch, "E900", {"start": v(-4.82, -18.76) * mm, "end": v(-4.59, -18.85) * mm});
            skLineSegment(sketch, "E901", {"start": v(-4.59, -18.85) * mm, "end": v(-4.43, -18.96) * mm});
            skLineSegment(sketch, "E902", {"start": v(-4.43, -18.96) * mm, "end": v(-4.39, -19) * mm});
            skLineSegment(sketch, "E903", {"start": v(-4.39, -19) * mm, "end": v(-4.35, -19.04) * mm});
            skLineSegment(sketch, "E904", {"start": v(-4.35, -19.04) * mm, "end": v(-4.25, -19.18) * mm});
            skLineSegment(sketch, "E905", {"start": v(-4.25, -19.18) * mm, "end": v(-4.17, -19.4) * mm});
            skLineSegment(sketch, "E906", {"start": v(-4.17, -19.4) * mm, "end": v(-4.14, -19.62) * mm});
            skLineSegment(sketch, "E907", {"start": v(-4.14, -19.62) * mm, "end": v(-4.17, -19.85) * mm});
            skLineSegment(sketch, "E908", {"start": v(-4.17, -19.85) * mm, "end": v(-4.24, -20.07) * mm});
            skLineSegment(sketch, "E909", {"start": v(-4.24, -20.07) * mm, "end": v(-4.36, -20.26) * mm});
            skLineSegment(sketch, "E910", {"start": v(-4.36, -20.26) * mm, "end": v(-4.52, -20.42) * mm});
            skLineSegment(sketch, "E911", {"start": v(-4.52, -20.42) * mm, "end": v(-4.67, -20.5) * mm});
            skLineSegment(sketch, "E912", {"start": v(-4.67, -20.5) * mm, "end": v(-4.73, -20.52) * mm});
            skLineSegment(sketch, "E913", {"start": v(-4.73, -20.52) * mm, "end": v(-4.8, -20.54) * mm});
            skLineSegment(sketch, "E914", {"start": v(-4.8, -20.54) * mm, "end": v(-5.55, -20.6) * mm});
            skLineSegment(sketch, "E915", {"start": v(-5.55, -20.6) * mm, "end": v(-5.62, -20.59) * mm});
            skLineSegment(sketch, "E916", {"start": v(-5.62, -20.59) * mm, "end": v(-5.65, -20.6) * mm});
            skLineSegment(sketch, "E917", {"start": v(-5.65, -20.6) * mm, "end": v(-5.73, -20.57) * mm});
            skLineSegment(sketch, "E918", {"start": v(-5.73, -20.57) * mm, "end": v(-5.8, -20.5) * mm});
            skLineSegment(sketch, "E919", {"start": v(-5.8, -20.5) * mm, "end": v(-5.84, -20.4) * mm});
            skLineSegment(sketch, "E920", {"start": v(-5.84, -20.4) * mm, "end": v(-5.85, -20.31) * mm});
            skLineSegment(sketch, "E921", {"start": v(-5.85, -20.31) * mm, "end": v(-5.85, -20.29) * mm});
            skLineSegment(sketch, "E922", {"start": v(-1.92, -19.23) * mm, "end": v(-1.75, -19.24) * mm});
            skLineSegment(sketch, "E923", {"start": v(-1.75, -19.24) * mm, "end": v(-1.22, -19.2) * mm});
            skLineSegment(sketch, "E924", {"start": v(-1.22, -19.2) * mm, "end": v(-0.52, -19.11) * mm});
            skLineSegment(sketch, "E925", {"start": v(-0.52, -19.11) * mm, "end": v(0.17, -19.06) * mm});
            skLineSegment(sketch, "E926", {"start": v(0.17, -19.06) * mm, "end": v(0.7, -19.1) * mm});
            skLineSegment(sketch, "E927", {"start": v(0.7, -19.1) * mm, "end": v(0.87, -19.15) * mm});
            skLineSegment(sketch, "E928", {"start": v(0.87, -19.15) * mm, "end": v(0.98, -19.17) * mm});
            skLineSegment(sketch, "E929", {"start": v(0.98, -19.17) * mm, "end": v(1.33, -19.27) * mm});
            skLineSegment(sketch, "E930", {"start": v(1.33, -19.27) * mm, "end": v(1.77, -19.46) * mm});
            skLineSegment(sketch, "E931", {"start": v(1.77, -19.46) * mm, "end": v(2.17, -19.71) * mm});
            skLineSegment(sketch, "E932", {"start": v(2.17, -19.71) * mm, "end": v(2.42, -19.97) * mm});
            skLineSegment(sketch, "E933", {"start": v(2.42, -19.97) * mm, "end": v(2.48, -20.07) * mm});
            skLineSegment(sketch, "E934", {"start": v(2.48, -20.07) * mm, "end": v(2.6, -20.25) * mm});
            skLineSegment(sketch, "E935", {"start": v(2.6, -20.25) * mm, "end": v(2.8, -20.92) * mm});
            skLineSegment(sketch, "E936", {"start": v(2.8, -20.92) * mm, "end": v(2.78, -21.85) * mm});
            skLineSegment(sketch, "E937", {"start": v(2.78, -21.85) * mm, "end": v(2.42, -22.7) * mm});
            skLineSegment(sketch, "E938", {"start": v(2.42, -22.7) * mm, "end": v(1.93, -23.2) * mm});
            skLineSegment(sketch, "E939", {"start": v(1.93, -23.2) * mm, "end": v(1.73, -23.3) * mm});
            skLineSegment(sketch, "E940", {"start": v(1.73, -23.3) * mm, "end": v(1.53, -23.37) * mm});
            skLineSegment(sketch, "E941", {"start": v(1.53, -23.37) * mm, "end": v(0.47, -23.56) * mm});
            skLineSegment(sketch, "E942", {"start": v(0.47, -23.56) * mm, "end": v(-0.6, -23.6) * mm});
            skLineSegment(sketch, "E943", {"start": v(-0.6, -23.6) * mm, "end": v(-0.82, -23.6) * mm});
            skLineSegment(sketch, "E944", {"start": v(-0.82, -23.6) * mm, "end": v(-0.9, -23.6) * mm});
            skLineSegment(sketch, "E945", {"start": v(-0.9, -23.6) * mm, "end": v(-1.33, -23.6) * mm});
            skLineSegment(sketch, "E946", {"start": v(-1.33, -23.6) * mm, "end": v(-1.74, -23.57) * mm});
            skLineSegment(sketch, "E947", {"start": v(-1.74, -23.57) * mm, "end": v(-1.83, -23.56) * mm});
            skLineSegment(sketch, "E948", {"start": v(-1.83, -23.56) * mm, "end": v(-1.77, -23.53) * mm});
            skLineSegment(sketch, "E949", {"start": v(-1.77, -23.53) * mm, "end": v(-1.22, -23.24) * mm});
            skLineSegment(sketch, "E950", {"start": v(-1.22, -23.24) * mm, "end": v(-1.16, -23.22) * mm});
            skLineSegment(sketch, "E951", {"start": v(-1.16, -23.22) * mm, "end": v(-1.14, -22.93) * mm});
            skLineSegment(sketch, "E952", {"start": v(-1.14, -22.93) * mm, "end": v(-1.13, -21.51) * mm});
            skLineSegment(sketch, "E953", {"start": v(-1.13, -21.51) * mm, "end": v(-1.23, -20.1) * mm});
            skLineSegment(sketch, "E954", {"start": v(-1.23, -20.1) * mm, "end": v(-1.27, -19.81) * mm});
            skLineSegment(sketch, "E955", {"start": v(-1.27, -19.81) * mm, "end": v(-1.28, -19.76) * mm});
            skLineSegment(sketch, "E956", {"start": v(-1.28, -19.76) * mm, "end": v(-1.36, -19.6) * mm});
            skLineSegment(sketch, "E957", {"start": v(-1.36, -19.6) * mm, "end": v(-1.52, -19.46) * mm});
            skLineSegment(sketch, "E958", {"start": v(-1.52, -19.46) * mm, "end": v(-1.73, -19.35) * mm});
            skLineSegment(sketch, "E959", {"start": v(-1.73, -19.35) * mm, "end": v(-1.88, -19.27) * mm});
            skLineSegment(sketch, "E960", {"start": v(-1.88, -19.27) * mm, "end": v(-1.92, -19.23) * mm});
            skLineSegment(sketch, "E961", {"start": v(-0.65, -19.3) * mm, "end": v(-0.52, -19.26) * mm});
            skLineSegment(sketch, "E962", {"start": v(-0.52, -19.26) * mm, "end": v(-0.11, -19.2) * mm});
            skLineSegment(sketch, "E963", {"start": v(-0.11, -19.2) * mm, "end": v(0.43, -19.23) * mm});
            skLineSegment(sketch, "E964", {"start": v(0.43, -19.23) * mm, "end": v(0.94, -19.4) * mm});
            skLineSegment(sketch, "E965", {"start": v(0.94, -19.4) * mm, "end": v(1.3, -19.6) * mm});
            skLineSegment(sketch, "E966", {"start": v(1.3, -19.6) * mm, "end": v(1.39, -19.7) * mm});
            skLineSegment(sketch, "E967", {"start": v(1.39, -19.7) * mm, "end": v(1.5, -19.78) * mm});
            skLineSegment(sketch, "E968", {"start": v(1.5, -19.78) * mm, "end": v(1.74, -20.1) * mm});
            skLineSegment(sketch, "E969", {"start": v(1.74, -20.1) * mm, "end": v(1.95, -20.58) * mm});
            skLineSegment(sketch, "E970", {"start": v(1.95, -20.58) * mm, "end": v(2.07, -21.1) * mm});
            skLineSegment(sketch, "E971", {"start": v(2.07, -21.1) * mm, "end": v(2.1, -21.5) * mm});
            skLineSegment(sketch, "E972", {"start": v(2.1, -21.5) * mm, "end": v(2.1, -21.62) * mm});
            skLineSegment(sketch, "E973", {"start": v(2.1, -21.62) * mm, "end": v(2.09, -21.73) * mm});
            skLineSegment(sketch, "E974", {"start": v(2.09, -21.73) * mm, "end": v(1.94, -22.25) * mm});
            skLineSegment(sketch, "E975", {"start": v(1.94, -22.25) * mm, "end": v(1.7, -22.73) * mm});
            skLineSegment(sketch, "E976", {"start": v(1.7, -22.73) * mm, "end": v(1.62, -22.82) * mm});
            skLineSegment(sketch, "E977", {"start": v(1.62, -22.82) * mm, "end": v(1.56, -22.88) * mm});
            skLineSegment(sketch, "E978", {"start": v(1.56, -22.88) * mm, "end": v(1.34, -23.06) * mm});
            skLineSegment(sketch, "E979", {"start": v(1.34, -23.06) * mm, "end": v(1, -23.26) * mm});
            skLineSegment(sketch, "E980", {"start": v(1, -23.26) * mm, "end": v(0.64, -23.36) * mm});
            skLineSegment(sketch, "E981", {"start": v(0.64, -23.36) * mm, "end": v(0.36, -23.37) * mm});
            skLineSegment(sketch, "E982", {"start": v(0.36, -23.37) * mm, "end": v(0.26, -23.35) * mm});
            skLineSegment(sketch, "E983", {"start": v(0.26, -23.35) * mm, "end": v(0.2, -23.34) * mm});
            skLineSegment(sketch, "E984", {"start": v(0.2, -23.34) * mm, "end": v(0.02, -23.26) * mm});
            skLineSegment(sketch, "E985", {"start": v(0.02, -23.26) * mm, "end": v(-0.2, -23.13) * mm});
            skLineSegment(sketch, "E986", {"start": v(-0.2, -23.13) * mm, "end": v(-0.38, -22.94) * mm});
            skLineSegment(sketch, "E987", {"start": v(-0.38, -22.94) * mm, "end": v(-0.46, -22.76) * mm});
            skLineSegment(sketch, "E988", {"start": v(-0.46, -22.76) * mm, "end": v(-0.46, -22.7) * mm});
            skLineSegment(sketch, "E989", {"start": v(-0.46, -22.7) * mm, "end": v(-0.48, -22.58) * mm});
            skLineSegment(sketch, "E990", {"start": v(-0.48, -22.58) * mm, "end": v(-0.59, -21.46) * mm});
            skLineSegment(sketch, "E991", {"start": v(-0.59, -21.46) * mm, "end": v(-0.59, -21.34) * mm});
            skLineSegment(sketch, "E992", {"start": v(-0.59, -21.34) * mm, "end": v(-0.6, -21.17) * mm});
            skLineSegment(sketch, "E993", {"start": v(-0.6, -21.17) * mm, "end": v(-0.64, -20.32) * mm});
            skLineSegment(sketch, "E994", {"start": v(-0.64, -20.32) * mm, "end": v(-0.66, -19.47) * mm});
            skLineSegment(sketch, "E995", {"start": v(-0.66, -19.47) * mm, "end": v(-0.65, -19.3) * mm});
            skCircle(sketch, "E996", {"center": v(0, 0) * mm, "radius": 18 * mm});
            skCircle(sketch, "E997", {"center": v(0, 0) * mm, "radius": 24.25 * mm});
            skCircle(sketch, "E998", {"center": v(0, 0) * mm, "radius": 25 * mm});
            skCircle(sketch, "E999.0", {"center": v(0, 0) * mm, "radius": 18.4 * mm});
            skSolve(sketch);
        }
        {
            var Q0;
            Q0=makeQuery(id+"F0.imprint","IMPRINT",FACE,{"disambiguationData":[TD([[makeQuery(id+"F0.imprint","IMPRINT",EDGE,{"derivedFrom":sQuery(id+"F0.wireOp",EDGE,"E997")}),-1.0]])]});
            var Q1;
            Q1=sQuery(id+"F0.wireOp",EDGE,"E998");
            var Q2;
            Q2=sQuery(id+"F0.wireOp",EDGE,"E997");
            extrude(context, id + "F1", {"entities" : qUnion([Q0]), "surfaceEntities" : qUnion([Q1, Q2]), "depth" : 4 * mm, "offsetDistance" : 25 * mm});
        }
        {
            var Q0;
            Q0 = qSketchRegion(id + "F0", true);
            var Q1;
            Q1=makeQuery(id+"F0.imprint","IMPRINT",FACE,{"disambiguationData":[TD([[makeQuery(id+"F0.imprint","IMPRINT",EDGE,{"derivedFrom":sQuery(id+"F0.wireOp",EDGE,"E0")}),1.0]])]});
            var Q2;
            Q2=makeQuery(id+"F0.imprint","IMPRINT",FACE,{"disambiguationData":[TD([[makeQuery(id+"F0.imprint","IMPRINT",EDGE,{"derivedFrom":sQuery(id+"F0.wireOp",EDGE,"E267")}),1.0]])]});
            var Q3;
            Q3=makeQuery(id+"F0.imprint","IMPRINT",FACE,{"disambiguationData":[TD([[makeQuery(id+"F0.imprint","IMPRINT",EDGE,{"derivedFrom":sQuery(id+"F0.wireOp",EDGE,"E627")}),-1.0]])]});
            var Q4;
            Q4=makeQuery(id+"F0.imprint","IMPRINT",FACE,{"disambiguationData":[TD([[makeQuery(id+"F0.imprint","IMPRINT",EDGE,{"derivedFrom":sQuery(id+"F0.wireOp",EDGE,"E893")}),-1.0]])]});
            var Q5;
            Q5=makeQuery(id+"F0.imprint","IMPRINT",FACE,{"disambiguationData":[TD([[makeQuery(id+"F0.imprint","IMPRINT",EDGE,{"derivedFrom":sQuery(id+"F0.wireOp",EDGE,"E961")}),-1.0]])]});
            var Q6;
            Q6=makeQuery(id+"F0.imprint","IMPRINT",FACE,{"disambiguationData":[TD([[makeQuery(id+"F0.imprint","IMPRINT",EDGE,{"derivedFrom":sQuery(id+"F0.wireOp",EDGE,"E675")}),-1.0]])]});
            var Q7;
            Q7=makeQuery(id+"F0.imprint","IMPRINT",FACE,{"disambiguationData":[TD([[makeQuery(id+"F0.imprint","IMPRINT",EDGE,{"derivedFrom":sQuery(id+"F0.wireOp",EDGE,"E433")}),-1.0]])]});
            var Q8;
            Q8=makeQuery(id+"F0.imprint","IMPRINT",FACE,{"disambiguationData":[TD([[makeQuery(id+"F0.imprint","IMPRINT",EDGE,{"derivedFrom":sQuery(id+"F0.wireOp",EDGE,"E463")}),-1.0]])]});
            extrude(context, id + "F2", {"entities" : qUnion([Q0, Q1, Q2, Q3, Q4, Q5, Q6, Q7, Q8]), "operationType" : NewBodyOperationType.ADD, "depth" : 3.4 * mm, "offsetDistance" : 25 * mm});
        }
        {
            var Q0;
            Q0=makeQuery(id+"F0.imprint","IMPRINT",FACE,{"disambiguationData":[TD([[makeQuery(id+"F0.imprint","IMPRINT",EDGE,{"derivedFrom":sQuery(id+"F0.wireOp",EDGE,"E490")}),-1.0]])]});
            var Q1;
            Q1=makeQuery(id+"F0.imprint","IMPRINT",FACE,{"disambiguationData":[TD([[makeQuery(id+"F0.imprint","IMPRINT",EDGE,{"derivedFrom":sQuery(id+"F0.wireOp",EDGE,"E701")}),-1.0]])]});
            var Q2;
            Q2=makeQuery(id+"F0.imprint","IMPRINT",FACE,{"disambiguationData":[TD([[makeQuery(id+"F0.imprint","IMPRINT",EDGE,{"derivedFrom":sQuery(id+"F0.wireOp",EDGE,"E781")}),-1.0]])]});
            var Q3;
            Q3=makeQuery(id+"F0.imprint","IMPRINT",FACE,{"disambiguationData":[TD([[makeQuery(id+"F0.imprint","IMPRINT",EDGE,{"derivedFrom":sQuery(id+"F0.wireOp",EDGE,"E536")}),-1.0]])]});
            var Q4;
            Q4=makeQuery(id+"F0.imprint","IMPRINT",FACE,{"disambiguationData":[TD([[makeQuery(id+"F0.imprint","IMPRINT",EDGE,{"derivedFrom":sQuery(id+"F0.wireOp",EDGE,"E267")}),-1.0]])]});
            var Q5;
            Q5=makeQuery(id+"F0.imprint","IMPRINT",FACE,{"disambiguationData":[TD([[makeQuery(id+"F0.imprint","IMPRINT",EDGE,{"derivedFrom":sQuery(id+"F0.wireOp",EDGE,"E344")}),-1.0]])]});
            var Q6;
            Q6=makeQuery(id+"F0.imprint","IMPRINT",FACE,{"disambiguationData":[TD([[makeQuery(id+"F0.imprint","IMPRINT",EDGE,{"derivedFrom":sQuery(id+"F0.wireOp",EDGE,"E0")}),-1.0]])]});
            var Q7;
            Q7=makeQuery(id+"F0.imprint","IMPRINT",FACE,{"disambiguationData":[TD([[makeQuery(id+"F0.imprint","IMPRINT",EDGE,{"derivedFrom":sQuery(id+"F0.wireOp",EDGE,"E168")}),-1.0]])]});
            var Q8;
            Q8=makeQuery(id+"F0.imprint","IMPRINT",FACE,{"disambiguationData":[TD([[makeQuery(id+"F0.imprint","IMPRINT",EDGE,{"derivedFrom":sQuery(id+"F0.wireOp",EDGE,"E76")}),-1.0]])]});
            var Q9;
            Q9=makeQuery(id+"F0.imprint","IMPRINT",FACE,{"disambiguationData":[TD([[makeQuery(id+"F0.imprint","IMPRINT",EDGE,{"derivedFrom":sQuery(id+"F0.wireOp",EDGE,"E922")}),-1.0]])]});
            extrude(context, id + "F3", {"entities" : qUnion([Q0, Q1, Q2, Q3, Q4, Q5, Q6, Q7, Q8, Q9]), "depth" : 4 * mm, "offsetDistance" : 25 * mm});
        }
        {
            var Q0;
            Q0=makeQuery(id+"F0.imprint","IMPRINT",FACE,{"disambiguationData":[TD([[makeQuery(id+"F0.imprint","IMPRINT",EDGE,{"derivedFrom":sQuery(id+"F0.wireOp",EDGE,"E996")}),-1.0]])]});
            var Q1;
            Q1=sQuery(id+"F0.wireOp",EDGE,"E996");
            var Q2;
            Q2=sQuery(id+"F0.wireOp",EDGE,"E999.0");
            extrude(context, id + "F4", {"entities" : qUnion([Q0]), "surfaceEntities" : qUnion([Q1, Q2]), "depth" : 4 * mm, "offsetDistance" : 25 * mm});
        }
        {
            var Q0;
            Q0=makeQuery(id+"F2.opExtrude","CAP_FACE",FACE,{"disambiguationData":[OSD([sQuery(id+"F0.wireOp",EDGE,"E267"),sQuery(id+"F0.wireOp",EDGE,"E268"),sQuery(id+"F0.wireOp",EDGE,"E269"),sQuery(id+"F0.wireOp",EDGE,"E270"),sQuery(id+"F0.wireOp",EDGE,"E271"),sQuery(id+"F0.wireOp",EDGE,"E272"),sQuery(id+"F0.wireOp",EDGE,"E273"),sQuery(id+"F0.wireOp",EDGE,"E274"),sQuery(id+"F0.wireOp",EDGE,"E275"),sQuery(id+"F0.wireOp",EDGE,"E276"),sQuery(id+"F0.wireOp",EDGE,"E277"),sQuery(id+"F0.wireOp",EDGE,"E278"),sQuery(id+"F0.wireOp",EDGE,"E279"),sQuery(id+"F0.wireOp",EDGE,"E280"),sQuery(id+"F0.wireOp",EDGE,"E281"),sQuery(id+"F0.wireOp",EDGE,"E282"),sQuery(id+"F0.wireOp",EDGE,"E283"),sQuery(id+"F0.wireOp",EDGE,"E284"),sQuery(id+"F0.wireOp",EDGE,"E285"),sQuery(id+"F0.wireOp",EDGE,"E286"),sQuery(id+"F0.wireOp",EDGE,"E287"),sQuery(id+"F0.wireOp",EDGE,"E288"),sQuery(id+"F0.wireOp",EDGE,"E289"),sQuery(id+"F0.wireOp",EDGE,"E290"),sQuery(id+"F0.wireOp",EDGE,"E291"),sQuery(id+"F0.wireOp",EDGE,"E292"),sQuery(id+"F0.wireOp",EDGE,"E293"),sQuery(id+"F0.wireOp",EDGE,"E294"),sQuery(id+"F0.wireOp",EDGE,"E295"),sQuery(id+"F0.wireOp",EDGE,"E296"),sQuery(id+"F0.wireOp",EDGE,"E297"),sQuery(id+"F0.wireOp",EDGE,"E298"),sQuery(id+"F0.wireOp",EDGE,"E299"),sQuery(id+"F0.wireOp",EDGE,"E300"),sQuery(id+"F0.wireOp",EDGE,"E301"),sQuery(id+"F0.wireOp",EDGE,"E302"),sQuery(id+"F0.wireOp",EDGE,"E303"),sQuery(id+"F0.wireOp",EDGE,"E304"),sQuery(id+"F0.wireOp",EDGE,"E305"),sQuery(id+"F0.wireOp",EDGE,"E306"),sQuery(id+"F0.wireOp",EDGE,"E307"),sQuery(id+"F0.wireOp",EDGE,"E308"),sQuery(id+"F0.wireOp",EDGE,"E309"),sQuery(id+"F0.wireOp",EDGE,"E310"),sQuery(id+"F0.wireOp",EDGE,"E311"),sQuery(id+"F0.wireOp",EDGE,"E312"),sQuery(id+"F0.wireOp",EDGE,"E313"),sQuery(id+"F0.wireOp",EDGE,"E314"),sQuery(id+"F0.wireOp",EDGE,"E315"),sQuery(id+"F0.wireOp",EDGE,"E316"),sQuery(id+"F0.wireOp",EDGE,"E317"),sQuery(id+"F0.wireOp",EDGE,"E318"),sQuery(id+"F0.wireOp",EDGE,"E319"),sQuery(id+"F0.wireOp",EDGE,"E320"),sQuery(id+"F0.wireOp",EDGE,"E321"),sQuery(id+"F0.wireOp",EDGE,"E322"),sQuery(id+"F0.wireOp",EDGE,"E323"),sQuery(id+"F0.wireOp",EDGE,"E324"),sQuery(id+"F0.wireOp",EDGE,"E325"),sQuery(id+"F0.wireOp",EDGE,"E326"),sQuery(id+"F0.wireOp",EDGE,"E327"),sQuery(id+"F0.wireOp",EDGE,"E328"),sQuery(id+"F0.wireOp",EDGE,"E329"),sQuery(id+"F0.wireOp",EDGE,"E330"),sQuery(id+"F0.wireOp",EDGE,"E331"),sQuery(id+"F0.wireOp",EDGE,"E332"),sQuery(id+"F0.wireOp",EDGE,"E333"),sQuery(id+"F0.wireOp",EDGE,"E334"),sQuery(id+"F0.wireOp",EDGE,"E335"),sQuery(id+"F0.wireOp",EDGE,"E336"),sQuery(id+"F0.wireOp",EDGE,"E337"),sQuery(id+"F0.wireOp",EDGE,"E338"),sQuery(id+"F0.wireOp",EDGE,"E339"),sQuery(id+"F0.wireOp",EDGE,"E340"),sQuery(id+"F0.wireOp",EDGE,"E341"),sQuery(id+"F0.wireOp",EDGE,"E342"),sQuery(id+"F0.wireOp",EDGE,"E343"),sQuery(id+"F0.wireOp",EDGE,"E344"),sQuery(id+"F0.wireOp",EDGE,"E345"),sQuery(id+"F0.wireOp",EDGE,"E346"),sQuery(id+"F0.wireOp",EDGE,"E347"),sQuery(id+"F0.wireOp",EDGE,"E348"),sQuery(id+"F0.wireOp",EDGE,"E349"),sQuery(id+"F0.wireOp",EDGE,"E350"),sQuery(id+"F0.wireOp",EDGE,"E351"),sQuery(id+"F0.wireOp",EDGE,"E352"),sQuery(id+"F0.wireOp",EDGE,"E353"),sQuery(id+"F0.wireOp",EDGE,"E354"),sQuery(id+"F0.wireOp",EDGE,"E355"),sQuery(id+"F0.wireOp",EDGE,"E356"),sQuery(id+"F0.wireOp",EDGE,"E357"),sQuery(id+"F0.wireOp",EDGE,"E358"),sQuery(id+"F0.wireOp",EDGE,"E359"),sQuery(id+"F0.wireOp",EDGE,"E360"),sQuery(id+"F0.wireOp",EDGE,"E361"),sQuery(id+"F0.wireOp",EDGE,"E362"),sQuery(id+"F0.wireOp",EDGE,"E363"),sQuery(id+"F0.wireOp",EDGE,"E364"),sQuery(id+"F0.wireOp",EDGE,"E365"),sQuery(id+"F0.wireOp",EDGE,"E366"),sQuery(id+"F0.wireOp",EDGE,"E367"),sQuery(id+"F0.wireOp",EDGE,"E368"),sQuery(id+"F0.wireOp",EDGE,"E369"),sQuery(id+"F0.wireOp",EDGE,"E370"),sQuery(id+"F0.wireOp",EDGE,"E371"),sQuery(id+"F0.wireOp",EDGE,"E372"),sQuery(id+"F0.wireOp",EDGE,"E373"),sQuery(id+"F0.wireOp",EDGE,"E374"),sQuery(id+"F0.wireOp",EDGE,"E375"),sQuery(id+"F0.wireOp",EDGE,"E376"),sQuery(id+"F0.wireOp",EDGE,"E377"),sQuery(id+"F0.wireOp",EDGE,"E378"),sQuery(id+"F0.wireOp",EDGE,"E379"),sQuery(id+"F0.wireOp",EDGE,"E380"),sQuery(id+"F0.wireOp",EDGE,"E381"),sQuery(id+"F0.wireOp",EDGE,"E382"),sQuery(id+"F0.wireOp",EDGE,"E383"),sQuery(id+"F0.wireOp",EDGE,"E384"),sQuery(id+"F0.wireOp",EDGE,"E385"),sQuery(id+"F0.wireOp",EDGE,"E386"),sQuery(id+"F0.wireOp",EDGE,"E387"),sQuery(id+"F0.wireOp",EDGE,"E388"),sQuery(id+"F0.wireOp",EDGE,"E389"),sQuery(id+"F0.wireOp",EDGE,"E390"),sQuery(id+"F0.wireOp",EDGE,"E391"),sQuery(id+"F0.wireOp",EDGE,"E392"),sQuery(id+"F0.wireOp",EDGE,"E393"),sQuery(id+"F0.wireOp",EDGE,"E394"),sQuery(id+"F0.wireOp",EDGE,"E395"),sQuery(id+"F0.wireOp",EDGE,"E396"),sQuery(id+"F0.wireOp",EDGE,"E397"),sQuery(id+"F0.wireOp",EDGE,"E398"),sQuery(id+"F0.wireOp",EDGE,"E399"),sQuery(id+"F0.wireOp",EDGE,"E400"),sQuery(id+"F0.wireOp",EDGE,"E401"),sQuery(id+"F0.wireOp",EDGE,"E402"),sQuery(id+"F0.wireOp",EDGE,"E403"),sQuery(id+"F0.wireOp",EDGE,"E404"),sQuery(id+"F0.wireOp",EDGE,"E405"),sQuery(id+"F0.wireOp",EDGE,"E406"),sQuery(id+"F0.wireOp",EDGE,"E407"),sQuery(id+"F0.wireOp",EDGE,"E408"),sQuery(id+"F0.wireOp",EDGE,"E409"),sQuery(id+"F0.wireOp",EDGE,"E410"),sQuery(id+"F0.wireOp",EDGE,"E411"),sQuery(id+"F0.wireOp",EDGE,"E412"),sQuery(id+"F0.wireOp",EDGE,"E413"),sQuery(id+"F0.wireOp",EDGE,"E414"),sQuery(id+"F0.wireOp",EDGE,"E415"),sQuery(id+"F0.wireOp",EDGE,"E416"),sQuery(id+"F0.wireOp",EDGE,"E417"),sQuery(id+"F0.wireOp",EDGE,"E418"),sQuery(id+"F0.wireOp",EDGE,"E419"),sQuery(id+"F0.wireOp",EDGE,"E420"),sQuery(id+"F0.wireOp",EDGE,"E421"),sQuery(id+"F0.wireOp",EDGE,"E422"),sQuery(id+"F0.wireOp",EDGE,"E423"),sQuery(id+"F0.wireOp",EDGE,"E424"),sQuery(id+"F0.wireOp",EDGE,"E425"),sQuery(id+"F0.wireOp",EDGE,"E426"),sQuery(id+"F0.wireOp",EDGE,"E427"),sQuery(id+"F0.wireOp",EDGE,"E428"),sQuery(id+"F0.wireOp",EDGE,"E429"),sQuery(id+"F0.wireOp",EDGE,"E430"),sQuery(id+"F0.wireOp",EDGE,"E431"),sQuery(id+"F0.wireOp",EDGE,"E432"),sQuery(id+"F0.wireOp",EDGE,"E996")])],"isStart":false});
            extrude(context, id + "F5", {"entities" : qUnion([Q0]), "operationType" : NewBodyOperationType.REMOVE, "oppositeDirection" : true, "depth" : .3 * mm, "offsetDistance" : 25 * mm});
        }
    });
